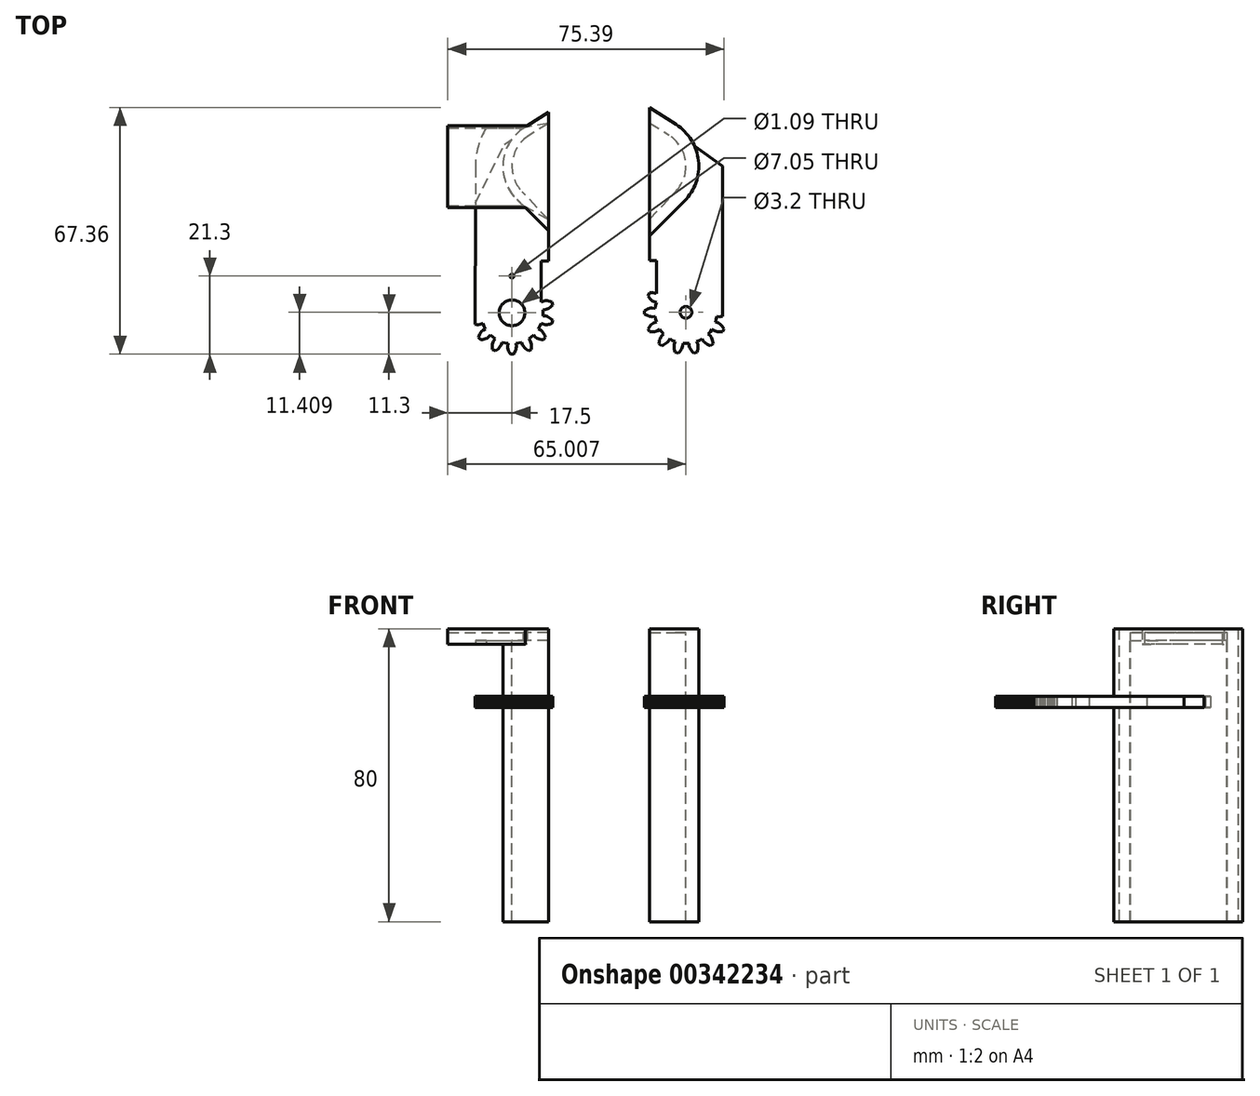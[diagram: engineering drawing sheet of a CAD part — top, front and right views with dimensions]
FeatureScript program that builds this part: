
annotation { "Feature Type Name" : "Feature", "Feature Type Description" : "" }
export const myFeature = defineFeature(function(context is Context, id is Id, definition is map)
    precondition{}
    {
        {
            var Q0;
            Q0=qCreatedBy(makeId("Top.planeOp"),FACE);
            var sketch = newSketch(context, id + "F0", { "sketchPlane" : qUnion([Q0])});
            skLineSegment(sketch, "E0", {"start": v(-11.89, -38.22) * mm, "end": v(-11.08, -38.37) * mm});
            skLineSegment(sketch, "E1", {"start": v(-11.08, -38.37) * mm, "end": v(-11.18, -39.18) * mm});
            skLineSegment(sketch, "E2", {"start": v(-11.18, -39.18) * mm, "end": v(-11.15, -39.59) * mm});
            skLineSegment(sketch, "E3", {"start": v(-11.15, -39.59) * mm, "end": v(-11.05, -40) * mm});
            skLineSegment(sketch, "E4", {"start": v(-11.05, -40) * mm, "end": v(-10.9, -40.42) * mm});
            skLineSegment(sketch, "E5", {"start": v(-10.9, -40.42) * mm, "end": v(-10.7, -40.84) * mm});
            skLineSegment(sketch, "E6", {"start": v(-10.7, -40.84) * mm, "end": v(-10.46, -41.25) * mm});
            skLineSegment(sketch, "E7", {"start": v(-10.46, -41.25) * mm, "end": v(-9.54, -41.25) * mm});
            skLineSegment(sketch, "E8", {"start": v(-9.54, -41.25) * mm, "end": v(-9.3, -40.84) * mm});
            skLineSegment(sketch, "E9", {"start": v(-9.3, -40.84) * mm, "end": v(-9.1, -40.42) * mm});
            skLineSegment(sketch, "E10", {"start": v(-9.1, -40.42) * mm, "end": v(-8.95, -40) * mm});
            skLineSegment(sketch, "E11", {"start": v(-8.95, -40) * mm, "end": v(-8.85, -39.59) * mm});
            skLineSegment(sketch, "E12", {"start": v(-8.85, -39.59) * mm, "end": v(-8.82, -39.18) * mm});
            skLineSegment(sketch, "E13", {"start": v(-8.82, -39.18) * mm, "end": v(-8.92, -38.37) * mm});
            skLineSegment(sketch, "E14", {"start": v(-8.92, -38.37) * mm, "end": v(-8.11, -38.22) * mm});
            skLineSegment(sketch, "E15", {"start": v(-8.11, -38.22) * mm, "end": v(-8.11, -38.22) * mm});
            skLineSegment(sketch, "E16", {"start": v(-8.11, -38.22) * mm, "end": v(-7.32, -38) * mm});
            skLineSegment(sketch, "E17", {"start": v(-7.32, -38) * mm, "end": v(-7.06, -38.78) * mm});
            skLineSegment(sketch, "E18", {"start": v(-7.06, -38.78) * mm, "end": v(-6.86, -39.13) * mm});
            skLineSegment(sketch, "E19", {"start": v(-6.86, -39.13) * mm, "end": v(-6.58, -39.46) * mm});
            skLineSegment(sketch, "E20", {"start": v(-6.58, -39.46) * mm, "end": v(-6.26, -39.77) * mm});
            skLineSegment(sketch, "E21", {"start": v(-6.26, -39.77) * mm, "end": v(-5.9, -40.06) * mm});
            skLineSegment(sketch, "E22", {"start": v(-5.9, -40.06) * mm, "end": v(-5.5, -40.33) * mm});
            skLineSegment(sketch, "E23", {"start": v(-5.5, -40.33) * mm, "end": v(-4.68, -39.94) * mm});
            skLineSegment(sketch, "E24", {"start": v(-4.68, -39.94) * mm, "end": v(-4.65, -39.46) * mm});
            skLineSegment(sketch, "E25", {"start": v(-4.65, -39.46) * mm, "end": v(-4.65, -39) * mm});
            skLineSegment(sketch, "E26", {"start": v(-4.7, -38.55) * mm, "end": v(-4.78, -38.13) * mm});
            skLineSegment(sketch, "E27", {"start": v(-4.78, -38.13) * mm, "end": v(-4.93, -37.75) * mm});
            skLineSegment(sketch, "E28", {"start": v(-4.93, -37.75) * mm, "end": v(-5.38, -37.07) * mm});
            skLineSegment(sketch, "E29", {"start": v(-4.09, -36.04) * mm, "end": v(-3.52, -36.62) * mm});
            skLineSegment(sketch, "E30", {"start": v(-3.18, -36.86) * mm, "end": v(-2.8, -37.04) * mm});
            skLineSegment(sketch, "E31", {"start": v(-2.37, -37.18) * mm, "end": v(-1.92, -37.28) * mm});
            skLineSegment(sketch, "E32", {"start": v(-1.05, -36.2) * mm, "end": v(-1.25, -35.78) * mm});
            skLineSegment(sketch, "E33", {"start": v(-1.25, -35.78) * mm, "end": v(-1.49, -35.4) * mm});
            skLineSegment(sketch, "E34", {"start": v(-2.05, -34.78) * mm, "end": v(-2.75, -34.36) * mm});
            skLineSegment(sketch, "E35", {"start": v(-2.03, -32.87) * mm, "end": v(-1.27, -33.15) * mm});
            skLineSegment(sketch, "E36", {"start": v(-20, -33.15) * mm, "end": v(-19.57, -33.2) * mm});
            skLineSegment(sketch, "E37", {"start": v(-19.57, -33.2) * mm, "end": v(-19.14, -33.22) * mm});
            skLineSegment(sketch, "E38", {"start": v(-19.14, -33.22) * mm, "end": v(-18.73, -33.15) * mm});
            skLineSegment(sketch, "E39", {"start": v(-18.73, -33.15) * mm, "end": v(-17.97, -32.87) * mm});
            skLineSegment(sketch, "E40", {"start": v(-17.97, -32.87) * mm, "end": v(-17.64, -33.63) * mm});
            skLineSegment(sketch, "E41", {"start": v(-17.64, -33.63) * mm, "end": v(-17.65, -33.63) * mm});
            skLineSegment(sketch, "E42", {"start": v(-17.65, -33.63) * mm, "end": v(-17.25, -34.36) * mm});
            skLineSegment(sketch, "E43", {"start": v(-17.25, -34.36) * mm, "end": v(-17.95, -34.78) * mm});
            skLineSegment(sketch, "E44", {"start": v(-17.95, -34.78) * mm, "end": v(-18.25, -35.06) * mm});
            skLineSegment(sketch, "E45", {"start": v(-18.25, -35.06) * mm, "end": v(-18.51, -35.4) * mm});
            skLineSegment(sketch, "E46", {"start": v(-18.51, -35.4) * mm, "end": v(-18.75, -35.78) * mm});
            skLineSegment(sketch, "E47", {"start": v(-18.75, -35.78) * mm, "end": v(-18.95, -36.2) * mm});
            skLineSegment(sketch, "E48", {"start": v(-18.95, -36.2) * mm, "end": v(-19.12, -36.64) * mm});
            skLineSegment(sketch, "E49", {"start": v(-19.12, -36.64) * mm, "end": v(-18.55, -37.36) * mm});
            skLineSegment(sketch, "E50", {"start": v(-18.55, -37.36) * mm, "end": v(-18.08, -37.28) * mm});
            skLineSegment(sketch, "E51", {"start": v(-18.08, -37.28) * mm, "end": v(-17.63, -37.18) * mm});
            skLineSegment(sketch, "E52", {"start": v(-17.63, -37.18) * mm, "end": v(-17.2, -37.04) * mm});
            skLineSegment(sketch, "E53", {"start": v(-17.2, -37.04) * mm, "end": v(-16.82, -36.86) * mm});
            skLineSegment(sketch, "E54", {"start": v(-16.82, -36.86) * mm, "end": v(-16.48, -36.62) * mm});
            skLineSegment(sketch, "E55", {"start": v(-16.48, -36.62) * mm, "end": v(-15.91, -36.04) * mm});
            skLineSegment(sketch, "E56", {"start": v(-15.91, -36.04) * mm, "end": v(-15.3, -36.58) * mm});
            skLineSegment(sketch, "E57", {"start": v(-15.3, -36.58) * mm, "end": v(-15.3, -36.58) * mm});
            skLineSegment(sketch, "E58", {"start": v(-15.3, -36.58) * mm, "end": v(-14.62, -37.07) * mm});
            skLineSegment(sketch, "E59", {"start": v(-14.62, -37.07) * mm, "end": v(-15.07, -37.75) * mm});
            skLineSegment(sketch, "E60", {"start": v(-15.07, -37.75) * mm, "end": v(-15.22, -38.13) * mm});
            skLineSegment(sketch, "E61", {"start": v(-15.22, -38.13) * mm, "end": v(-15.3, -38.55) * mm});
            skLineSegment(sketch, "E62", {"start": v(-15.3, -38.55) * mm, "end": v(-15.35, -39) * mm});
            skLineSegment(sketch, "E63", {"start": v(-15.35, -39) * mm, "end": v(-15.35, -39.46) * mm});
            skLineSegment(sketch, "E64", {"start": v(-15.35, -39.46) * mm, "end": v(-15.32, -39.94) * mm});
            skLineSegment(sketch, "E65", {"start": v(-15.32, -39.94) * mm, "end": v(-14.5, -40.33) * mm});
            skLineSegment(sketch, "E66", {"start": v(-14.5, -40.33) * mm, "end": v(-14.1, -40.06) * mm});
            skLineSegment(sketch, "E67", {"start": v(-14.1, -40.06) * mm, "end": v(-13.74, -39.77) * mm});
            skLineSegment(sketch, "E68", {"start": v(-13.74, -39.77) * mm, "end": v(-13.42, -39.46) * mm});
            skLineSegment(sketch, "E69", {"start": v(-13.42, -39.46) * mm, "end": v(-13.14, -39.13) * mm});
            skLineSegment(sketch, "E70", {"start": v(-13.14, -39.13) * mm, "end": v(-12.94, -38.78) * mm});
            skLineSegment(sketch, "E71", {"start": v(-12.94, -38.78) * mm, "end": v(-12.68, -38) * mm});
            skLineSegment(sketch, "E72", {"start": v(-12.68, -38) * mm, "end": v(-11.89, -38.22) * mm});
            skLineSegment(sketch, "E73", {"start": v(-11.89, -38.22) * mm, "end": v(-11.89, -38.22) * mm});
            skLineSegment(sketch, "E74", {"start": v(-2, -27.02) * mm, "end": v(-2, -15.8) * mm});
            skLineSegment(sketch, "E75", {"start": v(-4.65, -39) * mm, "end": v(-4.7, -38.55) * mm});
            skLineSegment(sketch, "E76", {"start": v(-5.38, -37.07) * mm, "end": v(-4.7, -36.58) * mm});
            skLineSegment(sketch, "E77", {"start": v(-4.7, -36.58) * mm, "end": v(-4.7, -36.58) * mm});
            skLineSegment(sketch, "E78", {"start": v(-4.7, -36.58) * mm, "end": v(-4.09, -36.04) * mm});
            skLineSegment(sketch, "E79", {"start": v(-3.52, -36.62) * mm, "end": v(-3.18, -36.86) * mm});
            skLineSegment(sketch, "E80", {"start": v(-2.8, -37.04) * mm, "end": v(-2.37, -37.18) * mm});
            skLineSegment(sketch, "E81", {"start": v(-1.92, -37.28) * mm, "end": v(-1.45, -37.36) * mm});
            skLineSegment(sketch, "E82", {"start": v(-1.45, -37.36) * mm, "end": v(-0.88, -36.64) * mm});
            skLineSegment(sketch, "E83", {"start": v(-0.88, -36.64) * mm, "end": v(-1.05, -36.2) * mm});
            skLineSegment(sketch, "E84", {"start": v(-1.49, -35.4) * mm, "end": v(-1.75, -35.06) * mm});
            skLineSegment(sketch, "E85", {"start": v(-1.75, -35.06) * mm, "end": v(-2.05, -34.78) * mm});
            skLineSegment(sketch, "E86", {"start": v(-2.75, -34.36) * mm, "end": v(-2.35, -33.63) * mm});
            skLineSegment(sketch, "E87", {"start": v(-2.35, -33.63) * mm, "end": v(-2.36, -33.63) * mm});
            skLineSegment(sketch, "E88", {"start": v(-2.36, -33.63) * mm, "end": v(-2.03, -32.87) * mm});
            skLineSegment(sketch, "E89", {"start": v(-1.27, -33.15) * mm, "end": v(-0.86, -33.22) * mm});
            skLineSegment(sketch, "E90", {"start": v(-0.86, -33.22) * mm, "end": v(-0.43, -33.2) * mm});
            skLineSegment(sketch, "E91", {"start": v(-0.43, -33.2) * mm, "end": v(0, -33.15) * mm});
            skLineSegment(sketch, "E92", {"start": v(0, -33.15) * mm, "end": v(0.46, -33.05) * mm});
            skLineSegment(sketch, "E93", {"start": v(0.46, -33.05) * mm, "end": v(0.92, -32.91) * mm});
            skLineSegment(sketch, "E94", {"start": v(0.92, -32.91) * mm, "end": v(1.12, -32.02) * mm});
            skLineSegment(sketch, "E95", {"start": v(1.12, -32.02) * mm, "end": v(0.77, -31.7) * mm});
            skLineSegment(sketch, "E96", {"start": v(0.77, -31.7) * mm, "end": v(0.4, -31.4) * mm});
            skLineSegment(sketch, "E97", {"start": v(0.4, -31.4) * mm, "end": v(0.03, -31.16) * mm});
            skLineSegment(sketch, "E98", {"start": v(0.03, -31.16) * mm, "end": v(-0.35, -30.97) * mm});
            skLineSegment(sketch, "E99", {"start": v(-0.35, -30.97) * mm, "end": v(-0.74, -30.85) * mm});
            skLineSegment(sketch, "E100", {"start": v(-0.74, -30.85) * mm, "end": v(-1.55, -30.77) * mm});
            skLineSegment(sketch, "E101", {"start": v(-1.55, -30.77) * mm, "end": v(-1.51, -29.95) * mm});
            skLineSegment(sketch, "E102", {"start": v(-1.51, -29.95) * mm, "end": v(-1.51, -29.95) * mm});
            skLineSegment(sketch, "E103", {"start": v(-1.51, -29.95) * mm, "end": v(-1.55, -29.13) * mm});
            skLineSegment(sketch, "E104", {"start": v(-1.55, -29.13) * mm, "end": v(-0.74, -29.05) * mm});
            skLineSegment(sketch, "E105", {"start": v(-0.74, -29.05) * mm, "end": v(-0.35, -28.93) * mm});
            skLineSegment(sketch, "E106", {"start": v(-0.35, -28.93) * mm, "end": v(0.03, -28.74) * mm});
            skLineSegment(sketch, "E107", {"start": v(0.03, -28.74) * mm, "end": v(0.4, -28.5) * mm});
            skLineSegment(sketch, "E108", {"start": v(0.4, -28.5) * mm, "end": v(0.77, -28.2) * mm});
            skLineSegment(sketch, "E109", {"start": v(0.77, -28.2) * mm, "end": v(1.12, -27.88) * mm});
            skLineSegment(sketch, "E110", {"start": v(1.12, -27.88) * mm, "end": v(0.92, -26.99) * mm});
            skLineSegment(sketch, "E111", {"start": v(0.92, -26.99) * mm, "end": v(0.46, -26.85) * mm});
            skLineSegment(sketch, "E112", {"start": v(0.46, -26.85) * mm, "end": v(0, -26.75) * mm});
            skLineSegment(sketch, "E113", {"start": v(0, -26.75) * mm, "end": v(-0.43, -26.69) * mm});
            skLineSegment(sketch, "E114", {"start": v(-0.43, -26.69) * mm, "end": v(-0.86, -26.68) * mm});
            skLineSegment(sketch, "E115", {"start": v(-0.86, -26.68) * mm, "end": v(-1.27, -26.75) * mm});
            skLineSegment(sketch, "E116", {"start": v(-1.27, -26.75) * mm, "end": v(-2, -27.02) * mm});
            skLineSegment(sketch, "E117", {"start": v(45.78, -31.73) * mm, "end": v(45.92, -30.92) * mm});
            skLineSegment(sketch, "E118", {"start": v(45.92, -30.92) * mm, "end": v(46.73, -31.02) * mm});
            skLineSegment(sketch, "E119", {"start": v(46.73, -31.02) * mm, "end": v(47.14, -31) * mm});
            skLineSegment(sketch, "E120", {"start": v(47.14, -31) * mm, "end": v(47.5, -30.9) * mm});
            skLineSegment(sketch, "E121", {"start": v(27.87, -31) * mm, "end": v(28.28, -31.02) * mm});
            skLineSegment(sketch, "E122", {"start": v(29.1, -30.92) * mm, "end": v(29.23, -31.73) * mm});
            skLineSegment(sketch, "E123", {"start": v(28.68, -32.78) * mm, "end": v(28.33, -32.99) * mm});
            skLineSegment(sketch, "E124", {"start": v(27.68, -33.58) * mm, "end": v(27.4, -33.94) * mm});
            skLineSegment(sketch, "E125", {"start": v(28.46, -35.2) * mm, "end": v(28.9, -35.15) * mm});
            skLineSegment(sketch, "E126", {"start": v(28.9, -35.15) * mm, "end": v(29.32, -35.06) * mm});
            skLineSegment(sketch, "E127", {"start": v(29.32, -35.06) * mm, "end": v(29.7, -34.9) * mm});
            skLineSegment(sketch, "E128", {"start": v(29.7, -34.9) * mm, "end": v(30.4, -34.46) * mm});
            skLineSegment(sketch, "E129", {"start": v(30.4, -34.46) * mm, "end": v(30.87, -35.13) * mm});
            skLineSegment(sketch, "E130", {"start": v(30.87, -35.13) * mm, "end": v(30.87, -35.13) * mm});
            skLineSegment(sketch, "E131", {"start": v(31.42, -35.75) * mm, "end": v(30.83, -36.32) * mm});
            skLineSegment(sketch, "E132", {"start": v(30.17, -37.92) * mm, "end": v(30.1, -38.4) * mm});
            skLineSegment(sketch, "E133", {"start": v(30.1, -38.4) * mm, "end": v(30.82, -38.96) * mm});
            skLineSegment(sketch, "E134", {"start": v(30.82, -38.96) * mm, "end": v(31.26, -38.8) * mm});
            skLineSegment(sketch, "E135", {"start": v(31.68, -38.59) * mm, "end": v(32.06, -38.35) * mm});
            skLineSegment(sketch, "E136", {"start": v(32.06, -38.35) * mm, "end": v(32.4, -38.1) * mm});
            skLineSegment(sketch, "E137", {"start": v(32.68, -37.8) * mm, "end": v(33.1, -37.1) * mm});
            skLineSegment(sketch, "E138", {"start": v(33.1, -37.1) * mm, "end": v(33.83, -37.49) * mm});
            skLineSegment(sketch, "E139", {"start": v(33.83, -37.49) * mm, "end": v(33.83, -37.49) * mm});
            skLineSegment(sketch, "E140", {"start": v(34.59, -37.8) * mm, "end": v(34.3, -38.58) * mm});
            skLineSegment(sketch, "E141", {"start": v(34.4, -40.3) * mm, "end": v(34.55, -40.76) * mm});
            skLineSegment(sketch, "E142", {"start": v(35.44, -40.96) * mm, "end": v(35.76, -40.61) * mm});
            skLineSegment(sketch, "E143", {"start": v(36.05, -40.25) * mm, "end": v(36.3, -39.88) * mm});
            skLineSegment(sketch, "E144", {"start": v(36.68, -38.29) * mm, "end": v(37.5, -38.33) * mm});
            skLineSegment(sketch, "E145", {"start": v(37.5, -38.33) * mm, "end": v(37.5, -38.33) * mm});
            skLineSegment(sketch, "E146", {"start": v(37.5, -38.33) * mm, "end": v(38.33, -38.29) * mm});
            skLineSegment(sketch, "E147", {"start": v(38.33, -38.29) * mm, "end": v(38.41, -39.1) * mm});
            skLineSegment(sketch, "E148", {"start": v(38.41, -39.1) * mm, "end": v(38.53, -39.5) * mm});
            skLineSegment(sketch, "E149", {"start": v(38.53, -39.5) * mm, "end": v(38.72, -39.88) * mm});
            skLineSegment(sketch, "E150", {"start": v(38.72, -39.88) * mm, "end": v(38.96, -40.25) * mm});
            skLineSegment(sketch, "E151", {"start": v(38.96, -40.25) * mm, "end": v(39.25, -40.61) * mm});
            skLineSegment(sketch, "E152", {"start": v(39.25, -40.61) * mm, "end": v(39.58, -40.96) * mm});
            skLineSegment(sketch, "E153", {"start": v(39.58, -40.96) * mm, "end": v(40.47, -40.76) * mm});
            skLineSegment(sketch, "E154", {"start": v(40.47, -40.76) * mm, "end": v(40.61, -40.3) * mm});
            skLineSegment(sketch, "E155", {"start": v(40.61, -40.3) * mm, "end": v(40.71, -39.85) * mm});
            skLineSegment(sketch, "E156", {"start": v(40.71, -39.85) * mm, "end": v(40.77, -39.4) * mm});
            skLineSegment(sketch, "E157", {"start": v(40.77, -39.4) * mm, "end": v(40.77, -38.98) * mm});
            skLineSegment(sketch, "E158", {"start": v(40.77, -38.98) * mm, "end": v(40.7, -38.58) * mm});
            skLineSegment(sketch, "E159", {"start": v(40.7, -38.58) * mm, "end": v(40.43, -37.8) * mm});
            skLineSegment(sketch, "E160", {"start": v(40.43, -37.8) * mm, "end": v(41.19, -37.49) * mm});
            skLineSegment(sketch, "E161", {"start": v(41.19, -37.49) * mm, "end": v(41.19, -37.49) * mm});
            skLineSegment(sketch, "E162", {"start": v(41.19, -37.49) * mm, "end": v(41.91, -37.1) * mm});
            skLineSegment(sketch, "E163", {"start": v(41.91, -37.1) * mm, "end": v(42.34, -37.8) * mm});
            skLineSegment(sketch, "E164", {"start": v(42.34, -37.8) * mm, "end": v(42.62, -38.1) * mm});
            skLineSegment(sketch, "E165", {"start": v(42.62, -38.1) * mm, "end": v(42.95, -38.35) * mm});
            skLineSegment(sketch, "E166", {"start": v(42.95, -38.35) * mm, "end": v(43.33, -38.59) * mm});
            skLineSegment(sketch, "E167", {"start": v(43.33, -38.59) * mm, "end": v(43.75, -38.8) * mm});
            skLineSegment(sketch, "E168", {"start": v(43.75, -38.8) * mm, "end": v(44.2, -38.96) * mm});
            skLineSegment(sketch, "E169", {"start": v(44.2, -38.96) * mm, "end": v(44.91, -38.4) * mm});
            skLineSegment(sketch, "E170", {"start": v(44.91, -38.4) * mm, "end": v(44.84, -37.92) * mm});
            skLineSegment(sketch, "E171", {"start": v(44.84, -37.92) * mm, "end": v(44.74, -37.47) * mm});
            skLineSegment(sketch, "E172", {"start": v(44.74, -37.47) * mm, "end": v(44.6, -37.05) * mm});
            skLineSegment(sketch, "E173", {"start": v(44.6, -37.05) * mm, "end": v(44.41, -36.66) * mm});
            skLineSegment(sketch, "E174", {"start": v(44.41, -36.66) * mm, "end": v(44.18, -36.32) * mm});
            skLineSegment(sketch, "E175", {"start": v(44.18, -36.32) * mm, "end": v(43.6, -35.75) * mm});
            skLineSegment(sketch, "E176", {"start": v(43.6, -35.75) * mm, "end": v(44.14, -35.13) * mm});
            skLineSegment(sketch, "E177", {"start": v(44.14, -35.13) * mm, "end": v(44.14, -35.13) * mm});
            skLineSegment(sketch, "E178", {"start": v(44.14, -35.13) * mm, "end": v(44.62, -34.46) * mm});
            skLineSegment(sketch, "E179", {"start": v(44.62, -34.46) * mm, "end": v(45.3, -34.9) * mm});
            skLineSegment(sketch, "E180", {"start": v(45.3, -34.9) * mm, "end": v(45.69, -35.06) * mm});
            skLineSegment(sketch, "E181", {"start": v(45.69, -35.06) * mm, "end": v(46.1, -35.15) * mm});
            skLineSegment(sketch, "E182", {"start": v(46.1, -35.15) * mm, "end": v(46.55, -35.2) * mm});
            skLineSegment(sketch, "E183", {"start": v(46.55, -35.2) * mm, "end": v(47.01, -35.2) * mm});
            skLineSegment(sketch, "E184", {"start": v(47.01, -35.2) * mm, "end": v(47.5, -35.16) * mm});
            skLineSegment(sketch, "E185", {"start": v(47.5, -35.16) * mm, "end": v(47.9, -34.33) * mm});
            skLineSegment(sketch, "E186", {"start": v(47.9, -34.33) * mm, "end": v(47.62, -33.94) * mm});
            skLineSegment(sketch, "E187", {"start": v(47.62, -33.94) * mm, "end": v(47.33, -33.58) * mm});
            skLineSegment(sketch, "E188", {"start": v(47.33, -33.58) * mm, "end": v(47.02, -33.26) * mm});
            skLineSegment(sketch, "E189", {"start": v(47.02, -33.26) * mm, "end": v(46.69, -32.99) * mm});
            skLineSegment(sketch, "E190", {"start": v(46.69, -32.99) * mm, "end": v(46.33, -32.78) * mm});
            skLineSegment(sketch, "E191", {"start": v(46.33, -32.78) * mm, "end": v(45.56, -32.52) * mm});
            skLineSegment(sketch, "E192", {"start": v(45.56, -32.52) * mm, "end": v(45.78, -31.73) * mm});
            skLineSegment(sketch, "E193", {"start": v(45.78, -31.73) * mm, "end": v(45.78, -31.73) * mm});
            skLineSegment(sketch, "E194", {"start": v(29.5, -24.7) * mm, "end": v(29.5, -15.7) * mm});
            skLineSegment(sketch, "E195", {"start": v(47.5, -30.9) * mm, "end": v(47.5, 10.1) * mm});
            skLineSegment(sketch, "E196", {"start": v(29.5, -24.7) * mm, "end": v(29.32, -24.62) * mm});
            skLineSegment(sketch, "E197", {"start": v(29.32, -24.62) * mm, "end": v(28.9, -24.53) * mm});
            skLineSegment(sketch, "E198", {"start": v(28.9, -24.53) * mm, "end": v(28.46, -24.5) * mm});
            skLineSegment(sketch, "E199", {"start": v(28.46, -24.5) * mm, "end": v(28, -24.49) * mm});
            skLineSegment(sketch, "E200", {"start": v(28, -24.49) * mm, "end": v(27.52, -24.53) * mm});
            skLineSegment(sketch, "E201", {"start": v(27.52, -24.53) * mm, "end": v(27.12, -25.35) * mm});
            skLineSegment(sketch, "E202", {"start": v(27.12, -25.35) * mm, "end": v(27.4, -25.75) * mm});
            skLineSegment(sketch, "E203", {"start": v(27.4, -25.75) * mm, "end": v(27.68, -26.1) * mm});
            skLineSegment(sketch, "E204", {"start": v(27.68, -26.1) * mm, "end": v(28, -26.43) * mm});
            skLineSegment(sketch, "E205", {"start": v(28, -26.43) * mm, "end": v(28.33, -26.7) * mm});
            skLineSegment(sketch, "E206", {"start": v(28.33, -26.7) * mm, "end": v(28.68, -26.9) * mm});
            skLineSegment(sketch, "E207", {"start": v(28.68, -26.9) * mm, "end": v(29.46, -27.16) * mm});
            skLineSegment(sketch, "E208", {"start": v(29.46, -27.16) * mm, "end": v(29.23, -27.95) * mm});
            skLineSegment(sketch, "E209", {"start": v(29.23, -27.95) * mm, "end": v(29.23, -27.95) * mm});
            skLineSegment(sketch, "E210", {"start": v(29.23, -27.95) * mm, "end": v(29.1, -28.77) * mm});
            skLineSegment(sketch, "E211", {"start": v(29.1, -28.77) * mm, "end": v(28.28, -28.66) * mm});
            skLineSegment(sketch, "E212", {"start": v(28.28, -28.66) * mm, "end": v(27.87, -28.7) * mm});
            skLineSegment(sketch, "E213", {"start": v(27.87, -28.7) * mm, "end": v(27.45, -28.8) * mm});
            skLineSegment(sketch, "E214", {"start": v(27.45, -28.8) * mm, "end": v(27.04, -28.94) * mm});
            skLineSegment(sketch, "E215", {"start": v(27.04, -28.94) * mm, "end": v(26.62, -29.14) * mm});
            skLineSegment(sketch, "E216", {"start": v(26.62, -29.14) * mm, "end": v(26.2, -29.38) * mm});
            skLineSegment(sketch, "E217", {"start": v(26.2, -30.3) * mm, "end": v(26.62, -30.54) * mm});
            skLineSegment(sketch, "E218", {"start": v(26.62, -30.54) * mm, "end": v(27.04, -30.74) * mm});
            skLineSegment(sketch, "E219", {"start": v(27.04, -30.74) * mm, "end": v(27.45, -30.9) * mm});
            skLineSegment(sketch, "E220", {"start": v(27.45, -30.9) * mm, "end": v(27.87, -31) * mm});
            skLineSegment(sketch, "E221", {"start": v(28.28, -31.02) * mm, "end": v(29.1, -30.92) * mm});
            skLineSegment(sketch, "E222", {"start": v(29.23, -31.73) * mm, "end": v(29.23, -31.73) * mm});
            skLineSegment(sketch, "E223", {"start": v(29.23, -31.73) * mm, "end": v(29.46, -32.52) * mm});
            skLineSegment(sketch, "E224", {"start": v(29.46, -32.52) * mm, "end": v(28.68, -32.78) * mm});
            skLineSegment(sketch, "E225", {"start": v(28.33, -32.99) * mm, "end": v(28, -33.26) * mm});
            skLineSegment(sketch, "E226", {"start": v(28, -33.26) * mm, "end": v(27.68, -33.58) * mm});
            skLineSegment(sketch, "E227", {"start": v(27.4, -33.94) * mm, "end": v(27.12, -34.33) * mm});
            skLineSegment(sketch, "E228", {"start": v(27.12, -34.33) * mm, "end": v(27.52, -35.16) * mm});
            skLineSegment(sketch, "E229", {"start": v(27.52, -35.16) * mm, "end": v(28, -35.2) * mm});
            skLineSegment(sketch, "E230", {"start": v(28, -35.2) * mm, "end": v(28.46, -35.2) * mm});
            skLineSegment(sketch, "E231", {"start": v(30.87, -35.13) * mm, "end": v(31.42, -35.75) * mm});
            skLineSegment(sketch, "E232", {"start": v(30.83, -36.32) * mm, "end": v(30.6, -36.66) * mm});
            skLineSegment(sketch, "E233", {"start": v(30.6, -36.66) * mm, "end": v(30.42, -37.05) * mm});
            skLineSegment(sketch, "E234", {"start": v(30.42, -37.05) * mm, "end": v(30.28, -37.47) * mm});
            skLineSegment(sketch, "E235", {"start": v(30.28, -37.47) * mm, "end": v(30.17, -37.92) * mm});
            skLineSegment(sketch, "E236", {"start": v(31.26, -38.8) * mm, "end": v(31.68, -38.59) * mm});
            skLineSegment(sketch, "E237", {"start": v(32.4, -38.1) * mm, "end": v(32.68, -37.8) * mm});
            skLineSegment(sketch, "E238", {"start": v(33.83, -37.49) * mm, "end": v(34.59, -37.8) * mm});
            skLineSegment(sketch, "E239", {"start": v(34.3, -38.58) * mm, "end": v(34.24, -38.98) * mm});
            skLineSegment(sketch, "E240", {"start": v(34.24, -38.98) * mm, "end": v(34.25, -39.4) * mm});
            skLineSegment(sketch, "E241", {"start": v(34.25, -39.4) * mm, "end": v(34.3, -39.85) * mm});
            skLineSegment(sketch, "E242", {"start": v(34.3, -39.85) * mm, "end": v(34.4, -40.3) * mm});
            skLineSegment(sketch, "E243", {"start": v(34.55, -40.76) * mm, "end": v(35.44, -40.96) * mm});
            skLineSegment(sketch, "E244", {"start": v(35.76, -40.61) * mm, "end": v(36.05, -40.25) * mm});
            skLineSegment(sketch, "E245", {"start": v(36.3, -39.88) * mm, "end": v(36.48, -39.5) * mm});
            skLineSegment(sketch, "E246", {"start": v(36.48, -39.5) * mm, "end": v(36.6, -39.1) * mm});
            skLineSegment(sketch, "E247", {"start": v(36.6, -39.1) * mm, "end": v(36.68, -38.29) * mm});
            skLineSegment(sketch, "E248", {"start": v(26.2, -29.38) * mm, "end": v(26.2, -30.3) * mm});
            skCircle(sketch, "E249", {"center": v(37.5, -29.84) * mm, "radius": 1.6 * mm});
            skCircle(sketch, "E250", {"center": v(-10, -29.95) * mm, "radius": 3.52 * mm});
            skCircle(sketch, "E251", {"center": v(-10, -19.95) * mm, "radius": 0.55 * mm});
            skLineSegment(sketch, "E252", {"start": v(97.08, -42.45) * mm, "end": v(97.9, -42.59) * mm});
            skLineSegment(sketch, "E253", {"start": v(97.9, -42.59) * mm, "end": v(97.8, -43.4) * mm});
            skLineSegment(sketch, "E254", {"start": v(97.8, -43.4) * mm, "end": v(97.82, -43.8) * mm});
            skLineSegment(sketch, "E255", {"start": v(97.82, -43.8) * mm, "end": v(97.92, -44.23) * mm});
            skLineSegment(sketch, "E256", {"start": v(97.92, -44.23) * mm, "end": v(98.07, -44.64) * mm});
            skLineSegment(sketch, "E257", {"start": v(98.07, -44.64) * mm, "end": v(98.27, -45.06) * mm});
            skLineSegment(sketch, "E258", {"start": v(98.27, -45.06) * mm, "end": v(98.51, -45.48) * mm});
            skLineSegment(sketch, "E259", {"start": v(98.51, -45.48) * mm, "end": v(99.43, -45.48) * mm});
            skLineSegment(sketch, "E260", {"start": v(99.43, -45.48) * mm, "end": v(99.67, -45.06) * mm});
            skLineSegment(sketch, "E261", {"start": v(99.67, -45.06) * mm, "end": v(99.87, -44.64) * mm});
            skLineSegment(sketch, "E262", {"start": v(99.87, -44.64) * mm, "end": v(100.02, -44.23) * mm});
            skLineSegment(sketch, "E263", {"start": v(100.02, -44.23) * mm, "end": v(100.12, -43.8) * mm});
            skLineSegment(sketch, "E264", {"start": v(100.12, -43.8) * mm, "end": v(100.15, -43.4) * mm});
            skLineSegment(sketch, "E265", {"start": v(100.15, -43.4) * mm, "end": v(100.05, -42.59) * mm});
            skLineSegment(sketch, "E266", {"start": v(100.05, -42.59) * mm, "end": v(100.86, -42.45) * mm});
            skLineSegment(sketch, "E267", {"start": v(100.86, -42.45) * mm, "end": v(100.86, -42.45) * mm});
            skLineSegment(sketch, "E268", {"start": v(100.86, -42.45) * mm, "end": v(101.65, -42.22) * mm});
            skLineSegment(sketch, "E269", {"start": v(101.65, -42.22) * mm, "end": v(101.91, -43) * mm});
            skLineSegment(sketch, "E270", {"start": v(101.91, -43) * mm, "end": v(102.12, -43.35) * mm});
            skLineSegment(sketch, "E271", {"start": v(102.12, -43.35) * mm, "end": v(102.39, -43.68) * mm});
            skLineSegment(sketch, "E272", {"start": v(102.39, -43.68) * mm, "end": v(102.7, -44) * mm});
            skLineSegment(sketch, "E273", {"start": v(102.7, -44) * mm, "end": v(103.07, -44.29) * mm});
            skLineSegment(sketch, "E274", {"start": v(103.07, -44.29) * mm, "end": v(103.46, -44.56) * mm});
            skLineSegment(sketch, "E275", {"start": v(103.46, -44.56) * mm, "end": v(104.29, -44.16) * mm});
            skLineSegment(sketch, "E276", {"start": v(104.29, -44.16) * mm, "end": v(104.32, -43.68) * mm});
            skLineSegment(sketch, "E277", {"start": v(104.32, -43.68) * mm, "end": v(104.32, -43.22) * mm});
            skLineSegment(sketch, "E278", {"start": v(104.28, -42.77) * mm, "end": v(104.19, -42.36) * mm});
            skLineSegment(sketch, "E279", {"start": v(104.19, -42.36) * mm, "end": v(104.04, -41.97) * mm});
            skLineSegment(sketch, "E280", {"start": v(104.04, -41.97) * mm, "end": v(103.6, -41.29) * mm});
            skLineSegment(sketch, "E281", {"start": v(104.88, -40.26) * mm, "end": v(105.45, -40.85) * mm});
            skLineSegment(sketch, "E282", {"start": v(105.79, -41.08) * mm, "end": v(106.18, -41.26) * mm});
            skLineSegment(sketch, "E283", {"start": v(106.6, -41.4) * mm, "end": v(107.05, -41.5) * mm});
            skLineSegment(sketch, "E284", {"start": v(107.92, -40.42) * mm, "end": v(107.72, -40) * mm});
            skLineSegment(sketch, "E285", {"start": v(107.72, -40) * mm, "end": v(107.48, -39.62) * mm});
            skLineSegment(sketch, "E286", {"start": v(106.92, -39) * mm, "end": v(106.22, -38.58) * mm});
            skLineSegment(sketch, "E287", {"start": v(106.94, -37.1) * mm, "end": v(107.7, -37.38) * mm});
            skLineSegment(sketch, "E288", {"start": v(88.96, -37.38) * mm, "end": v(89.4, -37.43) * mm});
            skLineSegment(sketch, "E289", {"start": v(89.4, -37.43) * mm, "end": v(89.83, -37.44) * mm});
            skLineSegment(sketch, "E290", {"start": v(89.83, -37.44) * mm, "end": v(90.24, -37.38) * mm});
            skLineSegment(sketch, "E291", {"start": v(90.24, -37.38) * mm, "end": v(91, -37.1) * mm});
            skLineSegment(sketch, "E292", {"start": v(91, -37.1) * mm, "end": v(91.33, -37.85) * mm});
            skLineSegment(sketch, "E293", {"start": v(91.33, -37.85) * mm, "end": v(91.33, -37.85) * mm});
            skLineSegment(sketch, "E294", {"start": v(91.33, -37.85) * mm, "end": v(91.72, -38.58) * mm});
            skLineSegment(sketch, "E295", {"start": v(91.72, -38.58) * mm, "end": v(91.02, -39) * mm});
            skLineSegment(sketch, "E296", {"start": v(91.02, -39) * mm, "end": v(90.72, -39.28) * mm});
            skLineSegment(sketch, "E297", {"start": v(90.72, -39.28) * mm, "end": v(90.46, -39.62) * mm});
            skLineSegment(sketch, "E298", {"start": v(90.46, -39.62) * mm, "end": v(90.23, -40) * mm});
            skLineSegment(sketch, "E299", {"start": v(90.23, -40) * mm, "end": v(90.02, -40.42) * mm});
            skLineSegment(sketch, "E300", {"start": v(90.02, -40.42) * mm, "end": v(89.85, -40.86) * mm});
            skLineSegment(sketch, "E301", {"start": v(89.85, -40.86) * mm, "end": v(90.42, -41.58) * mm});
            skLineSegment(sketch, "E302", {"start": v(90.42, -41.58) * mm, "end": v(90.9, -41.5) * mm});
            skLineSegment(sketch, "E303", {"start": v(90.9, -41.5) * mm, "end": v(91.34, -41.4) * mm});
            skLineSegment(sketch, "E304", {"start": v(91.34, -41.4) * mm, "end": v(91.77, -41.26) * mm});
            skLineSegment(sketch, "E305", {"start": v(91.77, -41.26) * mm, "end": v(92.15, -41.08) * mm});
            skLineSegment(sketch, "E306", {"start": v(92.15, -41.08) * mm, "end": v(92.5, -40.85) * mm});
            skLineSegment(sketch, "E307", {"start": v(92.5, -40.85) * mm, "end": v(93.06, -40.26) * mm});
            skLineSegment(sketch, "E308", {"start": v(93.06, -40.26) * mm, "end": v(93.68, -40.8) * mm});
            skLineSegment(sketch, "E309", {"start": v(93.68, -40.8) * mm, "end": v(93.68, -40.8) * mm});
            skLineSegment(sketch, "E310", {"start": v(93.68, -40.8) * mm, "end": v(94.35, -41.29) * mm});
            skLineSegment(sketch, "E311", {"start": v(94.35, -41.29) * mm, "end": v(93.9, -41.97) * mm});
            skLineSegment(sketch, "E312", {"start": v(93.9, -41.97) * mm, "end": v(93.75, -42.36) * mm});
            skLineSegment(sketch, "E313", {"start": v(93.75, -42.36) * mm, "end": v(93.66, -42.77) * mm});
            skLineSegment(sketch, "E314", {"start": v(93.66, -42.77) * mm, "end": v(93.62, -43.22) * mm});
            skLineSegment(sketch, "E315", {"start": v(93.62, -43.22) * mm, "end": v(93.62, -43.68) * mm});
            skLineSegment(sketch, "E316", {"start": v(93.62, -43.68) * mm, "end": v(93.65, -44.16) * mm});
            skLineSegment(sketch, "E317", {"start": v(93.65, -44.16) * mm, "end": v(94.48, -44.56) * mm});
            skLineSegment(sketch, "E318", {"start": v(94.48, -44.56) * mm, "end": v(94.87, -44.29) * mm});
            skLineSegment(sketch, "E319", {"start": v(94.87, -44.29) * mm, "end": v(95.24, -44) * mm});
            skLineSegment(sketch, "E320", {"start": v(95.24, -44) * mm, "end": v(95.55, -43.68) * mm});
            skLineSegment(sketch, "E321", {"start": v(95.55, -43.68) * mm, "end": v(95.83, -43.35) * mm});
            skLineSegment(sketch, "E322", {"start": v(95.83, -43.35) * mm, "end": v(96.03, -43) * mm});
            skLineSegment(sketch, "E323", {"start": v(96.03, -43) * mm, "end": v(96.29, -42.22) * mm});
            skLineSegment(sketch, "E324", {"start": v(96.29, -42.22) * mm, "end": v(97.08, -42.45) * mm});
            skLineSegment(sketch, "E325", {"start": v(97.08, -42.45) * mm, "end": v(97.08, -42.45) * mm});
            skLineSegment(sketch, "E326", {"start": v(98.97, -2.1) * mm, "end": v(98.97, 13.76) * mm});
            skArc(sketch, "E327", {"start": v(98.97, -2.1) * mm, "mid": v(99.35, -4.02) * mm, "end": v(100.44, -5.64) * mm});
            skLineSegment(sketch, "E328", {"start": v(106.97, -31.24) * mm, "end": v(106.97, -14.24) * mm});
            skArc(sketch, "E329", {"start": v(106.97, -14.24) * mm, "mid": v(106.6, -12.33) * mm, "end": v(105.5, -10.7) * mm});
            skLineSegment(sketch, "E330", {"start": v(108.97, 25.83) * mm, "end": v(108.97, 40.83) * mm});
            skLineSegment(sketch, "E331", {"start": v(108.97, 40.83) * mm, "end": v(106.04, 40.83) * mm});
            skArc(sketch, "E332", {"start": v(106.04, 40.83) * mm, "mid": v(104.13, 40.45) * mm, "end": v(102.5, 39.36) * mm});
            skLineSegment(sketch, "E333", {"start": v(88.96, -37.38) * mm, "end": v(88.97, 23.76) * mm});
            skLineSegment(sketch, "E334", {"start": v(102.5, 39.36) * mm, "end": v(90.43, 27.3) * mm});
            skArc(sketch, "E335", {"start": v(90.43, 27.3) * mm, "mid": v(89.35, 25.67) * mm, "end": v(88.97, 23.76) * mm});
            skLineSegment(sketch, "E336", {"start": v(108.97, 25.83) * mm, "end": v(100.44, 17.3) * mm});
            skArc(sketch, "E337", {"start": v(100.44, 17.3) * mm, "mid": v(99.35, 15.67) * mm, "end": v(98.97, 13.76) * mm});
            skLineSegment(sketch, "E338", {"start": v(100.44, -5.64) * mm, "end": v(105.5, -10.7) * mm});
            skLineSegment(sketch, "E339", {"start": v(104.32, -43.22) * mm, "end": v(104.28, -42.77) * mm});
            skLineSegment(sketch, "E340", {"start": v(103.6, -41.29) * mm, "end": v(104.26, -40.8) * mm});
            skLineSegment(sketch, "E341", {"start": v(104.26, -40.8) * mm, "end": v(104.26, -40.8) * mm});
            skLineSegment(sketch, "E342", {"start": v(104.26, -40.8) * mm, "end": v(104.88, -40.26) * mm});
            skLineSegment(sketch, "E343", {"start": v(105.45, -40.85) * mm, "end": v(105.79, -41.08) * mm});
            skLineSegment(sketch, "E344", {"start": v(106.18, -41.26) * mm, "end": v(106.6, -41.4) * mm});
            skLineSegment(sketch, "E345", {"start": v(107.05, -41.5) * mm, "end": v(107.52, -41.58) * mm});
            skLineSegment(sketch, "E346", {"start": v(107.52, -41.58) * mm, "end": v(108.1, -40.86) * mm});
            skLineSegment(sketch, "E347", {"start": v(108.1, -40.86) * mm, "end": v(107.92, -40.42) * mm});
            skLineSegment(sketch, "E348", {"start": v(107.48, -39.62) * mm, "end": v(107.22, -39.28) * mm});
            skLineSegment(sketch, "E349", {"start": v(107.22, -39.28) * mm, "end": v(106.92, -39) * mm});
            skLineSegment(sketch, "E350", {"start": v(106.22, -38.58) * mm, "end": v(106.62, -37.85) * mm});
            skLineSegment(sketch, "E351", {"start": v(106.62, -37.85) * mm, "end": v(106.62, -37.85) * mm});
            skLineSegment(sketch, "E352", {"start": v(106.62, -37.85) * mm, "end": v(106.94, -37.1) * mm});
            skLineSegment(sketch, "E353", {"start": v(107.7, -37.38) * mm, "end": v(108.1, -37.44) * mm});
            skLineSegment(sketch, "E354", {"start": v(108.1, -37.44) * mm, "end": v(108.54, -37.43) * mm});
            skLineSegment(sketch, "E355", {"start": v(108.54, -37.43) * mm, "end": v(108.98, -37.38) * mm});
            skLineSegment(sketch, "E356", {"start": v(108.98, -37.38) * mm, "end": v(109.43, -37.28) * mm});
            skLineSegment(sketch, "E357", {"start": v(109.43, -37.28) * mm, "end": v(109.9, -37.13) * mm});
            skLineSegment(sketch, "E358", {"start": v(109.9, -37.13) * mm, "end": v(110.1, -36.24) * mm});
            skLineSegment(sketch, "E359", {"start": v(110.1, -36.24) * mm, "end": v(109.74, -35.92) * mm});
            skLineSegment(sketch, "E360", {"start": v(109.74, -35.92) * mm, "end": v(109.38, -35.63) * mm});
            skLineSegment(sketch, "E361", {"start": v(109.38, -35.63) * mm, "end": v(109, -35.39) * mm});
            skLineSegment(sketch, "E362", {"start": v(109, -35.39) * mm, "end": v(108.62, -35.2) * mm});
            skLineSegment(sketch, "E363", {"start": v(108.62, -35.2) * mm, "end": v(108.23, -35.08) * mm});
            skLineSegment(sketch, "E364", {"start": v(108.23, -35.08) * mm, "end": v(107.42, -35) * mm});
            skLineSegment(sketch, "E365", {"start": v(107.42, -35) * mm, "end": v(107.46, -34.17) * mm});
            skLineSegment(sketch, "E366", {"start": v(107.46, -34.17) * mm, "end": v(107.46, -34.17) * mm});
            skLineSegment(sketch, "E367", {"start": v(107.46, -34.17) * mm, "end": v(107.42, -33.35) * mm});
            skLineSegment(sketch, "E368", {"start": v(107.42, -33.35) * mm, "end": v(108.23, -33.27) * mm});
            skLineSegment(sketch, "E369", {"start": v(108.23, -33.27) * mm, "end": v(108.62, -33.15) * mm});
            skLineSegment(sketch, "E370", {"start": v(108.62, -33.15) * mm, "end": v(109, -32.96) * mm});
            skLineSegment(sketch, "E371", {"start": v(109, -32.96) * mm, "end": v(109.38, -32.72) * mm});
            skLineSegment(sketch, "E372", {"start": v(109.38, -32.72) * mm, "end": v(109.74, -32.43) * mm});
            skLineSegment(sketch, "E373", {"start": v(109.74, -32.43) * mm, "end": v(110.1, -32.1) * mm});
            skLineSegment(sketch, "E374", {"start": v(110.1, -32.1) * mm, "end": v(109.9, -31.21) * mm});
            skLineSegment(sketch, "E375", {"start": v(109.9, -31.21) * mm, "end": v(109.43, -31.07) * mm});
            skLineSegment(sketch, "E376", {"start": v(109.43, -31.07) * mm, "end": v(108.98, -30.97) * mm});
            skLineSegment(sketch, "E377", {"start": v(108.98, -30.97) * mm, "end": v(108.54, -30.91) * mm});
            skLineSegment(sketch, "E378", {"start": v(108.54, -30.91) * mm, "end": v(108.1, -30.9) * mm});
            skLineSegment(sketch, "E379", {"start": v(108.1, -30.9) * mm, "end": v(107.7, -30.97) * mm});
            skLineSegment(sketch, "E380", {"start": v(107.7, -30.97) * mm, "end": v(106.97, -31.24) * mm});
            skLineSegment(sketch, "E381", {"start": v(150.9, -35.72) * mm, "end": v(151.04, -34.9) * mm});
            skLineSegment(sketch, "E382", {"start": v(151.04, -34.9) * mm, "end": v(151.85, -35) * mm});
            skLineSegment(sketch, "E383", {"start": v(151.85, -35) * mm, "end": v(152.25, -34.98) * mm});
            skLineSegment(sketch, "E384", {"start": v(152.25, -34.98) * mm, "end": v(152.62, -34.89) * mm});
            skLineSegment(sketch, "E385", {"start": v(132.98, -34.98) * mm, "end": v(133.4, -35) * mm});
            skLineSegment(sketch, "E386", {"start": v(134.2, -34.9) * mm, "end": v(134.35, -35.72) * mm});
            skLineSegment(sketch, "E387", {"start": v(133.8, -36.77) * mm, "end": v(133.44, -36.97) * mm});
            skLineSegment(sketch, "E388", {"start": v(132.8, -37.56) * mm, "end": v(132.5, -37.92) * mm});
            skLineSegment(sketch, "E389", {"start": v(133.57, -39.18) * mm, "end": v(134.02, -39.13) * mm});
            skLineSegment(sketch, "E390", {"start": v(134.02, -39.13) * mm, "end": v(134.44, -39.04) * mm});
            skLineSegment(sketch, "E391", {"start": v(134.44, -39.04) * mm, "end": v(134.82, -38.9) * mm});
            skLineSegment(sketch, "E392", {"start": v(134.82, -38.9) * mm, "end": v(135.5, -38.45) * mm});
            skLineSegment(sketch, "E393", {"start": v(135.5, -38.45) * mm, "end": v(135.98, -39.12) * mm});
            skLineSegment(sketch, "E394", {"start": v(135.98, -39.12) * mm, "end": v(135.98, -39.12) * mm});
            skLineSegment(sketch, "E395", {"start": v(136.53, -39.74) * mm, "end": v(135.94, -40.3) * mm});
            skLineSegment(sketch, "E396", {"start": v(135.28, -41.9) * mm, "end": v(135.21, -42.38) * mm});
            skLineSegment(sketch, "E397", {"start": v(135.21, -42.38) * mm, "end": v(135.93, -42.95) * mm});
            skLineSegment(sketch, "E398", {"start": v(135.93, -42.95) * mm, "end": v(136.37, -42.78) * mm});
            skLineSegment(sketch, "E399", {"start": v(136.8, -42.57) * mm, "end": v(137.17, -42.34) * mm});
            skLineSegment(sketch, "E400", {"start": v(137.17, -42.34) * mm, "end": v(137.5, -42.08) * mm});
            skLineSegment(sketch, "E401", {"start": v(137.79, -41.78) * mm, "end": v(138.21, -41.08) * mm});
            skLineSegment(sketch, "E402", {"start": v(138.21, -41.08) * mm, "end": v(138.94, -41.47) * mm});
            skLineSegment(sketch, "E403", {"start": v(138.94, -41.47) * mm, "end": v(138.94, -41.47) * mm});
            skLineSegment(sketch, "E404", {"start": v(139.7, -41.8) * mm, "end": v(139.42, -42.56) * mm});
            skLineSegment(sketch, "E405", {"start": v(139.51, -44.29) * mm, "end": v(139.66, -44.75) * mm});
            skLineSegment(sketch, "E406", {"start": v(140.55, -44.95) * mm, "end": v(140.88, -44.6) * mm});
            skLineSegment(sketch, "E407", {"start": v(141.16, -44.23) * mm, "end": v(141.4, -43.86) * mm});
            skLineSegment(sketch, "E408", {"start": v(141.8, -42.27) * mm, "end": v(142.62, -42.31) * mm});
            skLineSegment(sketch, "E409", {"start": v(142.62, -42.31) * mm, "end": v(142.62, -42.31) * mm});
            skLineSegment(sketch, "E410", {"start": v(142.62, -42.31) * mm, "end": v(143.44, -42.27) * mm});
            skLineSegment(sketch, "E411", {"start": v(143.44, -42.27) * mm, "end": v(143.52, -43.09) * mm});
            skLineSegment(sketch, "E412", {"start": v(143.52, -43.09) * mm, "end": v(143.64, -43.48) * mm});
            skLineSegment(sketch, "E413", {"start": v(143.64, -43.48) * mm, "end": v(143.83, -43.86) * mm});
            skLineSegment(sketch, "E414", {"start": v(143.83, -43.86) * mm, "end": v(144.07, -44.23) * mm});
            skLineSegment(sketch, "E415", {"start": v(144.07, -44.23) * mm, "end": v(144.36, -44.6) * mm});
            skLineSegment(sketch, "E416", {"start": v(144.36, -44.6) * mm, "end": v(144.69, -44.95) * mm});
            skLineSegment(sketch, "E417", {"start": v(144.69, -44.95) * mm, "end": v(145.58, -44.75) * mm});
            skLineSegment(sketch, "E418", {"start": v(145.58, -44.75) * mm, "end": v(145.72, -44.29) * mm});
            skLineSegment(sketch, "E419", {"start": v(145.72, -44.29) * mm, "end": v(145.82, -43.84) * mm});
            skLineSegment(sketch, "E420", {"start": v(145.82, -43.84) * mm, "end": v(145.88, -43.4) * mm});
            skLineSegment(sketch, "E421", {"start": v(145.88, -43.4) * mm, "end": v(145.88, -42.97) * mm});
            skLineSegment(sketch, "E422", {"start": v(145.88, -42.97) * mm, "end": v(145.82, -42.56) * mm});
            skLineSegment(sketch, "E423", {"start": v(145.82, -42.56) * mm, "end": v(145.54, -41.8) * mm});
            skLineSegment(sketch, "E424", {"start": v(145.54, -41.8) * mm, "end": v(146.3, -41.47) * mm});
            skLineSegment(sketch, "E425", {"start": v(146.3, -41.47) * mm, "end": v(146.3, -41.47) * mm});
            skLineSegment(sketch, "E426", {"start": v(146.3, -41.47) * mm, "end": v(147.03, -41.08) * mm});
            skLineSegment(sketch, "E427", {"start": v(147.03, -41.08) * mm, "end": v(147.45, -41.78) * mm});
            skLineSegment(sketch, "E428", {"start": v(147.45, -41.78) * mm, "end": v(147.73, -42.08) * mm});
            skLineSegment(sketch, "E429", {"start": v(147.73, -42.08) * mm, "end": v(148.07, -42.34) * mm});
            skLineSegment(sketch, "E430", {"start": v(148.07, -42.34) * mm, "end": v(148.45, -42.57) * mm});
            skLineSegment(sketch, "E431", {"start": v(148.45, -42.57) * mm, "end": v(148.86, -42.78) * mm});
            skLineSegment(sketch, "E432", {"start": v(148.86, -42.78) * mm, "end": v(149.3, -42.95) * mm});
            skLineSegment(sketch, "E433", {"start": v(149.3, -42.95) * mm, "end": v(150.02, -42.38) * mm});
            skLineSegment(sketch, "E434", {"start": v(150.02, -42.38) * mm, "end": v(149.95, -41.9) * mm});
            skLineSegment(sketch, "E435", {"start": v(149.95, -41.9) * mm, "end": v(149.85, -41.45) * mm});
            skLineSegment(sketch, "E436", {"start": v(149.85, -41.45) * mm, "end": v(149.7, -41.03) * mm});
            skLineSegment(sketch, "E437", {"start": v(149.7, -41.03) * mm, "end": v(149.53, -40.64) * mm});
            skLineSegment(sketch, "E438", {"start": v(149.53, -40.64) * mm, "end": v(149.3, -40.3) * mm});
            skLineSegment(sketch, "E439", {"start": v(149.3, -40.3) * mm, "end": v(148.7, -39.74) * mm});
            skLineSegment(sketch, "E440", {"start": v(148.7, -39.74) * mm, "end": v(149.25, -39.12) * mm});
            skLineSegment(sketch, "E441", {"start": v(149.25, -39.12) * mm, "end": v(149.25, -39.12) * mm});
            skLineSegment(sketch, "E442", {"start": v(149.25, -39.12) * mm, "end": v(149.73, -38.45) * mm});
            skLineSegment(sketch, "E443", {"start": v(149.73, -38.45) * mm, "end": v(150.42, -38.9) * mm});
            skLineSegment(sketch, "E444", {"start": v(150.42, -38.9) * mm, "end": v(150.8, -39.04) * mm});
            skLineSegment(sketch, "E445", {"start": v(150.8, -39.04) * mm, "end": v(151.22, -39.13) * mm});
            skLineSegment(sketch, "E446", {"start": v(151.22, -39.13) * mm, "end": v(151.66, -39.18) * mm});
            skLineSegment(sketch, "E447", {"start": v(151.66, -39.18) * mm, "end": v(152.13, -39.18) * mm});
            skLineSegment(sketch, "E448", {"start": v(152.13, -39.18) * mm, "end": v(152.6, -39.14) * mm});
            skLineSegment(sketch, "E449", {"start": v(152.6, -39.14) * mm, "end": v(153, -38.32) * mm});
            skLineSegment(sketch, "E450", {"start": v(153, -38.32) * mm, "end": v(152.73, -37.92) * mm});
            skLineSegment(sketch, "E451", {"start": v(152.73, -37.92) * mm, "end": v(152.44, -37.56) * mm});
            skLineSegment(sketch, "E452", {"start": v(152.44, -37.56) * mm, "end": v(152.13, -37.24) * mm});
            skLineSegment(sketch, "E453", {"start": v(152.13, -37.24) * mm, "end": v(151.8, -36.97) * mm});
            skLineSegment(sketch, "E454", {"start": v(151.8, -36.97) * mm, "end": v(151.44, -36.77) * mm});
            skLineSegment(sketch, "E455", {"start": v(151.44, -36.77) * mm, "end": v(150.67, -36.5) * mm});
            skLineSegment(sketch, "E456", {"start": v(150.67, -36.5) * mm, "end": v(150.9, -35.71) * mm});
            skLineSegment(sketch, "E457", {"start": v(150.9, -35.71) * mm, "end": v(150.9, -35.72) * mm});
            skLineSegment(sketch, "E458", {"start": v(134.62, -28.68) * mm, "end": v(134.62, -13.9) * mm});
            skLineSegment(sketch, "E459", {"start": v(132.62, 26.17) * mm, "end": v(132.62, 41.17) * mm});
            skLineSegment(sketch, "E460", {"start": v(132.62, 41.17) * mm, "end": v(135.55, 41.17) * mm});
            skLineSegment(sketch, "E461", {"start": v(152.62, -34.89) * mm, "end": v(152.62, 24.1) * mm});
            skArc(sketch, "E462", {"start": v(152.62, 24.1) * mm, "mid": v(152.24, 26.02) * mm, "end": v(151.15, 27.64) * mm});
            skLineSegment(sketch, "E463", {"start": v(139.08, 39.7) * mm, "end": v(151.15, 27.64) * mm});
            skArc(sketch, "E464", {"start": v(139.08, 39.7) * mm, "mid": v(137.46, 40.8) * mm, "end": v(135.55, 41.17) * mm});
            skLineSegment(sketch, "E465", {"start": v(132.62, 26.17) * mm, "end": v(141.15, 17.64) * mm});
            skArc(sketch, "E466", {"start": v(142.62, 14.1) * mm, "mid": v(142.24, 16.02) * mm, "end": v(141.15, 17.64) * mm});
            skLineSegment(sketch, "E467", {"start": v(142.62, 14.1) * mm, "end": v(142.62, -1.76) * mm});
            skArc(sketch, "E468", {"start": v(141.15, -5.3) * mm, "mid": v(142.24, -3.67) * mm, "end": v(142.62, -1.76) * mm});
            skLineSegment(sketch, "E469", {"start": v(141.15, -5.3) * mm, "end": v(136.08, -10.36) * mm});
            skArc(sketch, "E470", {"start": v(136.08, -10.36) * mm, "mid": v(135, -11.98) * mm, "end": v(134.62, -13.9) * mm});
            skLineSegment(sketch, "E471", {"start": v(134.62, -28.68) * mm, "end": v(134.44, -28.6) * mm});
            skLineSegment(sketch, "E472", {"start": v(134.44, -28.6) * mm, "end": v(134.02, -28.52) * mm});
            skLineSegment(sketch, "E473", {"start": v(134.02, -28.52) * mm, "end": v(133.57, -28.48) * mm});
            skLineSegment(sketch, "E474", {"start": v(133.57, -28.48) * mm, "end": v(133.11, -28.47) * mm});
            skLineSegment(sketch, "E475", {"start": v(133.11, -28.47) * mm, "end": v(132.63, -28.51) * mm});
            skLineSegment(sketch, "E476", {"start": v(132.63, -28.51) * mm, "end": v(132.24, -29.33) * mm});
            skLineSegment(sketch, "E477", {"start": v(132.24, -29.33) * mm, "end": v(132.5, -29.73) * mm});
            skLineSegment(sketch, "E478", {"start": v(132.5, -29.73) * mm, "end": v(132.8, -30.1) * mm});
            skLineSegment(sketch, "E479", {"start": v(132.8, -30.1) * mm, "end": v(133.1, -30.41) * mm});
            skLineSegment(sketch, "E480", {"start": v(133.1, -30.41) * mm, "end": v(133.44, -30.68) * mm});
            skLineSegment(sketch, "E481", {"start": v(133.44, -30.68) * mm, "end": v(133.8, -30.89) * mm});
            skLineSegment(sketch, "E482", {"start": v(133.8, -30.89) * mm, "end": v(134.57, -31.14) * mm});
            skLineSegment(sketch, "E483", {"start": v(134.57, -31.14) * mm, "end": v(134.35, -31.94) * mm});
            skLineSegment(sketch, "E484", {"start": v(134.35, -31.94) * mm, "end": v(134.35, -31.94) * mm});
            skLineSegment(sketch, "E485", {"start": v(134.35, -31.94) * mm, "end": v(134.2, -32.75) * mm});
            skLineSegment(sketch, "E486", {"start": v(134.2, -32.75) * mm, "end": v(133.4, -32.65) * mm});
            skLineSegment(sketch, "E487", {"start": v(133.4, -32.65) * mm, "end": v(132.98, -32.68) * mm});
            skLineSegment(sketch, "E488", {"start": v(132.98, -32.68) * mm, "end": v(132.57, -32.78) * mm});
            skLineSegment(sketch, "E489", {"start": v(132.57, -32.78) * mm, "end": v(132.15, -32.93) * mm});
            skLineSegment(sketch, "E490", {"start": v(132.15, -32.93) * mm, "end": v(131.73, -33.13) * mm});
            skLineSegment(sketch, "E491", {"start": v(131.73, -33.13) * mm, "end": v(131.31, -33.37) * mm});
            skLineSegment(sketch, "E492", {"start": v(131.31, -34.28) * mm, "end": v(131.73, -34.52) * mm});
            skLineSegment(sketch, "E493", {"start": v(131.73, -34.52) * mm, "end": v(132.15, -34.72) * mm});
            skLineSegment(sketch, "E494", {"start": v(132.15, -34.72) * mm, "end": v(132.57, -34.88) * mm});
            skLineSegment(sketch, "E495", {"start": v(132.57, -34.88) * mm, "end": v(132.98, -34.98) * mm});
            skLineSegment(sketch, "E496", {"start": v(133.4, -35) * mm, "end": v(134.2, -34.9) * mm});
            skLineSegment(sketch, "E497", {"start": v(134.35, -35.72) * mm, "end": v(134.35, -35.71) * mm});
            skLineSegment(sketch, "E498", {"start": v(134.35, -35.71) * mm, "end": v(134.57, -36.5) * mm});
            skLineSegment(sketch, "E499", {"start": v(134.57, -36.5) * mm, "end": v(133.8, -36.77) * mm});
            skLineSegment(sketch, "E500", {"start": v(133.44, -36.97) * mm, "end": v(133.1, -37.24) * mm});
            skLineSegment(sketch, "E501", {"start": v(133.1, -37.24) * mm, "end": v(132.8, -37.56) * mm});
            skLineSegment(sketch, "E502", {"start": v(132.5, -37.92) * mm, "end": v(132.24, -38.32) * mm});
            skLineSegment(sketch, "E503", {"start": v(132.24, -38.32) * mm, "end": v(132.63, -39.14) * mm});
            skLineSegment(sketch, "E504", {"start": v(132.63, -39.14) * mm, "end": v(133.11, -39.18) * mm});
            skLineSegment(sketch, "E505", {"start": v(133.11, -39.18) * mm, "end": v(133.57, -39.18) * mm});
            skLineSegment(sketch, "E506", {"start": v(135.98, -39.12) * mm, "end": v(136.53, -39.74) * mm});
            skLineSegment(sketch, "E507", {"start": v(135.94, -40.3) * mm, "end": v(135.71, -40.64) * mm});
            skLineSegment(sketch, "E508", {"start": v(135.71, -40.64) * mm, "end": v(135.53, -41.03) * mm});
            skLineSegment(sketch, "E509", {"start": v(135.53, -41.03) * mm, "end": v(135.39, -41.45) * mm});
            skLineSegment(sketch, "E510", {"start": v(135.39, -41.45) * mm, "end": v(135.28, -41.9) * mm});
            skLineSegment(sketch, "E511", {"start": v(136.37, -42.78) * mm, "end": v(136.8, -42.57) * mm});
            skLineSegment(sketch, "E512", {"start": v(137.5, -42.08) * mm, "end": v(137.79, -41.78) * mm});
            skLineSegment(sketch, "E513", {"start": v(138.94, -41.47) * mm, "end": v(139.7, -41.8) * mm});
            skLineSegment(sketch, "E514", {"start": v(139.42, -42.56) * mm, "end": v(139.35, -42.97) * mm});
            skLineSegment(sketch, "E515", {"start": v(139.35, -42.97) * mm, "end": v(139.36, -43.4) * mm});
            skLineSegment(sketch, "E516", {"start": v(139.36, -43.4) * mm, "end": v(139.41, -43.84) * mm});
            skLineSegment(sketch, "E517", {"start": v(139.41, -43.84) * mm, "end": v(139.51, -44.29) * mm});
            skLineSegment(sketch, "E518", {"start": v(139.66, -44.75) * mm, "end": v(140.55, -44.95) * mm});
            skLineSegment(sketch, "E519", {"start": v(140.88, -44.6) * mm, "end": v(141.16, -44.23) * mm});
            skLineSegment(sketch, "E520", {"start": v(141.4, -43.86) * mm, "end": v(141.6, -43.48) * mm});
            skLineSegment(sketch, "E521", {"start": v(141.6, -43.48) * mm, "end": v(141.71, -43.09) * mm});
            skLineSegment(sketch, "E522", {"start": v(141.71, -43.09) * mm, "end": v(141.8, -42.27) * mm});
            skLineSegment(sketch, "E523", {"start": v(131.31, -33.37) * mm, "end": v(131.31, -34.28) * mm});
            skCircle(sketch, "E524", {"center": v(142.62, -33.83) * mm, "radius": 0.75 * mm});
            skCircle(sketch, "E525", {"center": v(98.97, -34.17) * mm, "radius": 2.22 * mm});
            skCircle(sketch, "E526", {"center": v(98.97, -26.05) * mm, "radius": 0.55 * mm});
            skPoint(sketch, "E527.endSnap0", {"position": v(-2, -18.52) * mm});
            skLineSegment(sketch, "E528", {"start": v(-2, -15.8) * mm, "end": v(-0.05, -15.8) * mm});
            skLineSegment(sketch, "E529", {"start": v(27.56, -15.7) * mm, "end": v(27.56, -5.9) * mm});
            skLineSegment(sketch, "E530", {"start": v(-0.05, -15.8) * mm, "end": v(-0.05, -6) * mm});
            skLineSegment(sketch, "E531.trimOffspring", {"start": v(27.56, -15.7) * mm, "end": v(29.5, -15.7) * mm});
            skPoint(sketch, "E532.orphan", {"position": v(-2, -10.02) * mm});
            skLineSegment(sketch, "E533", {"start": v(-0.05, 23) * mm, "end": v(-0.05, 30) * mm});
            skLineSegment(sketch, "E534", {"start": v(27.56, 23.1) * mm, "end": v(27.56, 30.1) * mm});
            skArc(sketch, "E535", {"start": v(47.5, 10.1) * mm, "mid": v(41.67, 24.23) * mm, "end": v(27.56, 30.1) * mm});
            skPoint(sketch, "E536.endSnap0", {"position": v(-0.05, 10) * mm});
            skLineSegment(sketch, "E537", {"start": v(-20, 10) * mm, "end": v(-20, -33.15) * mm});
            skArc(sketch, "E538.trimOffspring", {"start": v(-0.05, 30) * mm, "mid": v(-14.16, 24.12) * mm, "end": v(-20, 10) * mm});
            skArc(sketch, "E539.trimOffspring", {"start": v(35.52, 2.57) * mm, "mid": v(38.42, 11.48) * mm, "end": v(33.4, 19.4) * mm});
            skLineSegment(sketch, "E540", {"start": v(27.56, -5.9) * mm, "end": v(35.52, 2.57) * mm});
            skLineSegment(sketch, "E541", {"start": v(27.56, 23.1) * mm, "end": v(33.4, 19.4) * mm});
            skArc(sketch, "E542", {"start": v(37.03, 0.54) * mm, "mid": v(40.93, 11.55) * mm, "end": v(34.79, 21.48) * mm});
            skLineSegment(sketch, "E543.MirrorCS", {"start": v(-0.05, -9) * mm, "end": v(-9.52, 0.43) * mm});
            skLineSegment(sketch, "E544", {"start": v(27.56, 26.1) * mm, "end": v(34.79, 21.48) * mm});
            skLineSegment(sketch, "E545", {"start": v(37.03, 0.54) * mm, "end": v(27.56, -9) * mm});
            skLineSegment(sketch, "E546", {"start": v(-0.05, -6) * mm, "end": v(-0.05, 23) * mm});
            skLineSegment(sketch, "E547", {"start": v(27.56, 23.1) * mm, "end": v(27.56, -9) * mm});
            skLineSegment(sketch, "E548", {"start": v(-129.43, -31.07) * mm, "end": v(-129.43, -28.07) * mm});
            skLineSegment(sketch, "E549", {"start": v(-129.43, 0.93) * mm, "end": v(-129.43, 3.93) * mm});
            skArc(sketch, "E550", {"start": v(-92.35, -21.53) * mm, "mid": v(-88.45, -10.52) * mm, "end": v(-94.6, -0.6) * mm});
            skLineSegment(sketch, "E551.MirrorCS", {"start": v(-129.43, -31.07) * mm, "end": v(-138.9, -21.63) * mm});
            skLineSegment(sketch, "E552", {"start": v(-101.82, 4.04) * mm, "end": v(-94.6, -0.6) * mm});
            skArc(sketch, "E553.trimOffspring", {"start": v(-136.66, -0.7) * mm, "mid": v(-142.8, -10.63) * mm, "end": v(-138.9, -21.63) * mm});
            skLineSegment(sketch, "E554.MirrorCS", {"start": v(-129.43, 3.93) * mm, "end": v(-136.66, -0.7) * mm});
            skLineSegment(sketch, "E555", {"start": v(-92.35, -21.53) * mm, "end": v(-101.82, -31.06) * mm});
            skLineSegment(sketch, "E556", {"start": v(-129.43, -28.07) * mm, "end": v(-129.43, 0.93) * mm});
            skLineSegment(sketch, "E557", {"start": v(-101.82, 1.04) * mm, "end": v(-101.82, -31.06) * mm});
            skLineSegment(sketch, "E558", {"start": v(-101.82, 4.04) * mm, "end": v(-101.82, 1.04) * mm});
            skLineSegment(sketch, "E559", {"start": v(-20, 0) * mm, "end": v(-12.1, 15.98) * mm});
            skLineSegment(sketch, "E560", {"start": v(47.5, 10.1) * mm, "end": v(39.85, 15.58) * mm});
            skLineSegment(sketch, "E561", {"start": v(-10, -19.95) * mm, "end": v(-10, -29.95) * mm});
            skLineSegment(sketch, "E562.0", {"start": v(0.68, -5.31) * mm, "end": v(-7.28, 3.15) * mm});
            skArc(sketch, "E562.1", {"start": v(-5.36, 18.44) * mm, "mid": v(-9.92, 11.25) * mm, "end": v(-7.28, 3.15) * mm});
            skLineSegment(sketch, "E562.2", {"start": v(0.49, 22.16) * mm, "end": v(-5.36, 18.44) * mm});
            skLineSegment(sketch, "E563.0", {"start": v(26.83, -5.2) * mm, "end": v(34.8, 3.26) * mm});
            skArc(sketch, "E563.1", {"start": v(34.8, 3.26) * mm, "mid": v(37.43, 11.35) * mm, "end": v(32.87, 18.55) * mm});
            skLineSegment(sketch, "E563.2", {"start": v(27.02, 22.26) * mm, "end": v(32.87, 18.55) * mm});
            skLineSegment(sketch, "E564.0", {"start": v(0.66, -8.3) * mm, "end": v(-8.82, 1.14) * mm});
            skArc(sketch, "E564.1", {"start": v(-6.74, 20.53) * mm, "mid": v(-12.43, 11.33) * mm, "end": v(-8.82, 1.14) * mm});
            skLineSegment(sketch, "E564.2", {"start": v(0.49, 25.16) * mm, "end": v(-6.74, 20.53) * mm});
            skLineSegment(sketch, "E565", {"start": v(-12.1, 15.98) * mm, "end": v(-10.12, 17.33) * mm});
            skLineSegment(sketch, "E566", {"start": v(-0.05, 21.82) * mm, "end": v(-6.74, 20.53) * mm});
            skLineSegment(sketch, "E567", {"start": v(-0.05, -4.54) * mm, "end": v(-7, -0.68) * mm});
            skLineSegment(sketch, "E568", {"start": v(-12.5, 10) * mm, "end": v(-27.5, 10) * mm});
            skLineSegment(sketch, "E569", {"start": v(-27.5, 10) * mm, "end": v(-27.5, 20.53) * mm});
            skLineSegment(sketch, "E570", {"start": v(-27.5, 20.53) * mm, "end": v(-6.74, 20.53) * mm});
            skLineSegment(sketch, "E571", {"start": v(-27.5, 10) * mm, "end": v(-27.5, -0.68) * mm});
            skLineSegment(sketch, "E572", {"start": v(-27.5, -0.68) * mm, "end": v(-7, -0.68) * mm});
            skLineSegment(sketch, "E573", {"start": v(-27.5, 20.53) * mm, "end": v(-27.5, 21.13) * mm});
            skLineSegment(sketch, "E574", {"start": v(-27.5, 21.13) * mm, "end": v(-5.8, 21.13) * mm});
            skLineSegment(sketch, "E575", {"start": v(-27.5, -0.68) * mm, "end": v(-27.5, -1.28) * mm});
            skLineSegment(sketch, "E576", {"start": v(-27.5, -1.28) * mm, "end": v(-6.4, -1.28) * mm});
            skSolve(sketch);
        }
        {
            var Q0;
            Q0=makeQuery(id+"F0.imprint","IMPRINT",FACE,{"disambiguationData":[TD([[makeQuery(id+"F0.imprint","IMPRINT",EDGE,{"derivedFrom":sQuery(id+"F0.wireOp",EDGE,"E0")}),1.0]])]});
            var Q1;
            Q1=makeQuery(id+"F0.imprint","IMPRINT",FACE,{"disambiguationData":[TD([[makeQuery(id+"F0.imprint","IMPRINT",EDGE,{"derivedFrom":sQuery(id+"F0.wireOp",EDGE,"E117")}),1.0]])]});
            var Q2;
            {var subQ5=sQuery(id+"F0.wireOp",EDGE,"E543.MirrorCS");Q2=makeQuery(id+"F0.imprint","IMPRINT",FACE,{"disambiguationData":[TD([[makeQuery(id+"F0.imprint","IMPRINT",EDGE,{"derivedFrom":subQ5}),-1.0]])]});}
            var Q3;
            {var subQ7=sQuery(id+"F0.wireOp",EDGE,"E559");var subQ8=sQuery(id+"F0.wireOp",EDGE,"E537");var subQ9=makeQuery(id+"F0.imprint","INTERSECT",VERTEX,{"derivedFrom":[subQ8,subQ7]});Q3=makeQuery(id+"F0.imprint","IMPRINT",FACE,{"disambiguationData":[TD([[makeQuery(id+"F0.imprint","IMPRINT",EDGE,{"disambiguationData":[TD([[subQ9,-1.0]])],"derivedFrom":subQ8}),1.0]])]});}
            var Q4;
            {var subQ0=sQuery(id+"F0.wireOp",EDGE,"E565");Q4=makeQuery(id+"F0.imprint","IMPRINT",FACE,{"disambiguationData":[TD([[makeQuery(id+"F0.imprint","IMPRINT",EDGE,{"derivedFrom":subQ0}),-1.0]])]});}
            var Q5;
            {var subQ0=sQuery(id+"F0.wireOp",EDGE,"E576");var subQ1=sQuery(id+"F0.wireOp",EDGE,"E537");var subQ2=makeQuery(id+"F0.imprint","INTERSECT",VERTEX,{"derivedFrom":[subQ1,subQ0]});Q5=makeQuery(id+"F0.imprint","IMPRINT",FACE,{"disambiguationData":[TD([[makeQuery(id+"F0.imprint","IMPRINT",EDGE,{"disambiguationData":[TD([[subQ2,1.0]])],"derivedFrom":subQ1}),1.0]])]});}
            extrude(context, id + "F1", {"entities" : qUnion([Q0, Q1, Q2, Q3, Q4, Q5]), "endBound" : BoundingType.SYMMETRIC, "depth" : 3 * mm});
        }
        {
            var Q0;
            {var subQ12=sQuery(id+"F0.wireOp",EDGE,"E562.1");Q0=makeQuery(id+"F0.imprint","IMPRINT",FACE,{"disambiguationData":[TD([[makeQuery(id+"F0.imprint","IMPRINT",EDGE,{"derivedFrom":subQ12}),-1.0]])]});}
            var Q1;
            Q1=makeQuery(id+"F0.imprint","IMPRINT",FACE,{"disambiguationData":[TD([[makeQuery(id+"F0.imprint","IMPRINT",EDGE,{"derivedFrom":sQuery(id+"F0.wireOp",EDGE,"E539.trimOffspring")}),1.0]])]});
            var Q2;
            Q2=makeQuery(id+"F0.imprint","IMPRINT",FACE,{"disambiguationData":[TD([[makeQuery(id+"F0.imprint","IMPRINT",EDGE,{"derivedFrom":sQuery(id+"F0.wireOp",EDGE,"E539.trimOffspring")}),-1.0]])]});
            var Q3;
            {var subQ5=sQuery(id+"F0.wireOp",EDGE,"E566");Q3=makeQuery(id+"F0.imprint","IMPRINT",FACE,{"disambiguationData":[TD([[makeQuery(id+"F0.imprint","IMPRINT",EDGE,{"derivedFrom":subQ5}),-1.0]])]});}
            var Q4;
            {var subQ5=sQuery(id+"F0.wireOp",EDGE,"E567");Q4=makeQuery(id+"F0.imprint","IMPRINT",FACE,{"disambiguationData":[TD([[makeQuery(id+"F0.imprint","IMPRINT",EDGE,{"derivedFrom":subQ5}),1.0]])]});}
            var Q5;
            {var subQ5=sQuery(id+"F0.wireOp",EDGE,"E562.1");Q5=makeQuery(id+"F0.imprint","IMPRINT",FACE,{"disambiguationData":[TD([[makeQuery(id+"F0.imprint","IMPRINT",EDGE,{"derivedFrom":subQ5}),1.0]])]});}
            var Q6;
            {var subQ5=sQuery(id+"F0.wireOp",EDGE,"E563.1");Q6=makeQuery(id+"F0.imprint","IMPRINT",FACE,{"disambiguationData":[TD([[makeQuery(id+"F0.imprint","IMPRINT",EDGE,{"derivedFrom":subQ5}),1.0]])]});}
            var Q7;
            {var subQ0=sQuery(id+"F0.wireOp",EDGE,"E565");Q7=makeQuery(id+"F0.imprint","IMPRINT",FACE,{"disambiguationData":[TD([[makeQuery(id+"F0.imprint","IMPRINT",EDGE,{"derivedFrom":subQ0}),1.0]])]});}
            var Q8;
            {var subQ5=sQuery(id+"F0.wireOp",EDGE,"E569");Q8=makeQuery(id+"F0.imprint","IMPRINT",FACE,{"disambiguationData":[TD([[makeQuery(id+"F0.imprint","IMPRINT",EDGE,{"derivedFrom":subQ5}),-1.0]])]});}
            var Q9;
            {var subQ3=sQuery(id+"F0.wireOp",EDGE,"E571");Q9=makeQuery(id+"F0.imprint","IMPRINT",FACE,{"disambiguationData":[TD([[makeQuery(id+"F0.imprint","IMPRINT",EDGE,{"derivedFrom":subQ3}),1.0]])]});}
            var Q10;
            {var subQ1=sQuery(id+"F0.wireOp",EDGE,"E537");var subQ3=sQuery(id+"F0.wireOp",EDGE,"E559");var subQ4=makeQuery(id+"F0.imprint","INTERSECT",VERTEX,{"derivedFrom":[subQ1,subQ3]});Q10=makeQuery(id+"F0.imprint","IMPRINT",FACE,{"disambiguationData":[TD([[makeQuery(id+"F0.imprint","IMPRINT",EDGE,{"disambiguationData":[TD([[subQ4,-1.0]])],"derivedFrom":subQ3}),1.0]])]});}
            var Q11;
            {var subQ7=sQuery(id+"F0.wireOp",EDGE,"E559");var subQ8=sQuery(id+"F0.wireOp",EDGE,"E537");var subQ9=makeQuery(id+"F0.imprint","INTERSECT",VERTEX,{"derivedFrom":[subQ8,subQ7]});Q11=makeQuery(id+"F0.imprint","IMPRINT",FACE,{"disambiguationData":[TD([[makeQuery(id+"F0.imprint","IMPRINT",EDGE,{"disambiguationData":[TD([[subQ9,-1.0]])],"derivedFrom":subQ8}),1.0]])]});}
            var Q12;
            {var subQ0=sQuery(id+"F0.wireOp",EDGE,"E565");Q12=makeQuery(id+"F0.imprint","IMPRINT",FACE,{"disambiguationData":[TD([[makeQuery(id+"F0.imprint","IMPRINT",EDGE,{"derivedFrom":subQ0}),-1.0]])]});}
            var Q13;
            {var subQ0=sQuery(id+"F0.wireOp",EDGE,"E574");var subQ1=sQuery(id+"F0.wireOp",EDGE,"E538.trimOffspring");var subQ2=makeQuery(id+"F0.imprint","INTERSECT",VERTEX,{"derivedFrom":[subQ1,subQ0]});Q13=makeQuery(id+"F0.imprint","IMPRINT",FACE,{"disambiguationData":[TD([[makeQuery(id+"F0.imprint","IMPRINT",EDGE,{"disambiguationData":[TD([[subQ2,-1.0]])],"derivedFrom":subQ1}),1.0]])]});}
            var Q14;
            {var subQ5=sQuery(id+"F0.wireOp",EDGE,"E573");Q14=makeQuery(id+"F0.imprint","IMPRINT",FACE,{"disambiguationData":[TD([[makeQuery(id+"F0.imprint","IMPRINT",EDGE,{"derivedFrom":subQ5}),-1.0]])]});}
            var Q15;
            {var subQ0=sQuery(id+"F0.wireOp",EDGE,"E572");var subQ1=sQuery(id+"F0.wireOp",EDGE,"E543.MirrorCS");var subQ2=makeQuery(id+"F0.imprint","INTERSECT",VERTEX,{"derivedFrom":[subQ1,subQ0]});Q15=makeQuery(id+"F0.imprint","IMPRINT",FACE,{"disambiguationData":[TD([[makeQuery(id+"F0.imprint","IMPRINT",EDGE,{"disambiguationData":[TD([[subQ2,1.0]])],"derivedFrom":subQ1}),-1.0]])]});}
            var Q16;
            {var subQ0=sQuery(id+"F0.wireOp",EDGE,"E576");var subQ1=sQuery(id+"F0.wireOp",EDGE,"E537");var subQ2=makeQuery(id+"F0.imprint","INTERSECT",VERTEX,{"derivedFrom":[subQ1,subQ0]});Q16=makeQuery(id+"F0.imprint","IMPRINT",FACE,{"disambiguationData":[TD([[makeQuery(id+"F0.imprint","IMPRINT",EDGE,{"disambiguationData":[TD([[subQ2,1.0]])],"derivedFrom":subQ1}),1.0]])]});}
            var Q17;
            {var subQ5=sQuery(id+"F0.wireOp",EDGE,"E575");Q17=makeQuery(id+"F0.imprint","IMPRINT",FACE,{"disambiguationData":[TD([[makeQuery(id+"F0.imprint","IMPRINT",EDGE,{"derivedFrom":subQ5}),1.0]])]});}
            extrude(context, id + "F2", {"entities" : qUnion([Q0, Q1, Q2, Q3, Q4, Q5, Q6, Q7, Q8, Q9, Q10, Q11, Q12, Q13, Q14, Q15, Q16, Q17]), "depth" : 20 * mm});
        }
        {
            var Q0;
            {var subQ12=sQuery(id+"F0.wireOp",EDGE,"E562.1");Q0=makeQuery(id+"F0.imprint","IMPRINT",FACE,{"disambiguationData":[TD([[makeQuery(id+"F0.imprint","IMPRINT",EDGE,{"derivedFrom":subQ12}),-1.0]])]});}
            var Q1;
            Q1=makeQuery(id+"F0.imprint","IMPRINT",FACE,{"disambiguationData":[TD([[makeQuery(id+"F0.imprint","IMPRINT",EDGE,{"derivedFrom":sQuery(id+"F0.wireOp",EDGE,"E539.trimOffspring")}),1.0]])]});
            var Q2;
            Q2=makeQuery(id+"F0.imprint","IMPRINT",FACE,{"disambiguationData":[TD([[makeQuery(id+"F0.imprint","IMPRINT",EDGE,{"derivedFrom":sQuery(id+"F0.wireOp",EDGE,"E539.trimOffspring")}),-1.0]])]});
            var Q3;
            {var subQ5=sQuery(id+"F0.wireOp",EDGE,"E567");Q3=makeQuery(id+"F0.imprint","IMPRINT",FACE,{"disambiguationData":[TD([[makeQuery(id+"F0.imprint","IMPRINT",EDGE,{"derivedFrom":subQ5}),1.0]])]});}
            var Q4;
            {var subQ5=sQuery(id+"F0.wireOp",EDGE,"E566");Q4=makeQuery(id+"F0.imprint","IMPRINT",FACE,{"disambiguationData":[TD([[makeQuery(id+"F0.imprint","IMPRINT",EDGE,{"derivedFrom":subQ5}),-1.0]])]});}
            extrude(context, id + "F3", {"entities" : qUnion([Q0, Q1, Q2, Q3, Q4]), "operationType" : NewBodyOperationType.ADD, "oppositeDirection" : true, "depth" : 60 * mm});
        }
        {
            var Q0;
            {var subQ5=sQuery(id+"F0.wireOp",EDGE,"E562.1");Q0=makeQuery(id+"F0.imprint","IMPRINT",FACE,{"disambiguationData":[TD([[makeQuery(id+"F0.imprint","IMPRINT",EDGE,{"derivedFrom":subQ5}),-1.0]])]});}
            var Q1;
            {var subQ5=sQuery(id+"F0.wireOp",EDGE,"E562.1");Q1=makeQuery(id+"F0.imprint","IMPRINT",FACE,{"disambiguationData":[TD([[makeQuery(id+"F0.imprint","IMPRINT",EDGE,{"derivedFrom":subQ5}),1.0]])]});}
            var Q2;
            {var subQ5=sQuery(id+"F0.wireOp",EDGE,"E563.1");Q2=makeQuery(id+"F0.imprint","IMPRINT",FACE,{"disambiguationData":[TD([[makeQuery(id+"F0.imprint","IMPRINT",EDGE,{"derivedFrom":subQ5}),1.0]])]});}
            var Q3;
            {var subQ3=sQuery(id+"F0.wireOp",EDGE,"E571");Q3=makeQuery(id+"F0.imprint","IMPRINT",FACE,{"disambiguationData":[TD([[makeQuery(id+"F0.imprint","IMPRINT",EDGE,{"derivedFrom":subQ3}),1.0]])]});}
            var Q4;
            {var subQ1=sQuery(id+"F0.wireOp",EDGE,"E537");var subQ3=sQuery(id+"F0.wireOp",EDGE,"E559");var subQ4=makeQuery(id+"F0.imprint","INTERSECT",VERTEX,{"derivedFrom":[subQ1,subQ3]});Q4=makeQuery(id+"F0.imprint","IMPRINT",FACE,{"disambiguationData":[TD([[makeQuery(id+"F0.imprint","IMPRINT",EDGE,{"disambiguationData":[TD([[subQ4,-1.0]])],"derivedFrom":subQ3}),1.0]])]});}
            var Q5;
            {var subQ7=sQuery(id+"F0.wireOp",EDGE,"E559");var subQ8=sQuery(id+"F0.wireOp",EDGE,"E537");var subQ9=makeQuery(id+"F0.imprint","INTERSECT",VERTEX,{"derivedFrom":[subQ8,subQ7]});Q5=makeQuery(id+"F0.imprint","IMPRINT",FACE,{"disambiguationData":[TD([[makeQuery(id+"F0.imprint","IMPRINT",EDGE,{"disambiguationData":[TD([[subQ9,-1.0]])],"derivedFrom":subQ8}),1.0]])]});}
            var Q6;
            {var subQ0=sQuery(id+"F0.wireOp",EDGE,"E565");Q6=makeQuery(id+"F0.imprint","IMPRINT",FACE,{"disambiguationData":[TD([[makeQuery(id+"F0.imprint","IMPRINT",EDGE,{"derivedFrom":subQ0}),-1.0]])]});}
            var Q7;
            {var subQ0=sQuery(id+"F0.wireOp",EDGE,"E565");Q7=makeQuery(id+"F0.imprint","IMPRINT",FACE,{"disambiguationData":[TD([[makeQuery(id+"F0.imprint","IMPRINT",EDGE,{"derivedFrom":subQ0}),1.0]])]});}
            var Q8;
            {var subQ5=sQuery(id+"F0.wireOp",EDGE,"E569");Q8=makeQuery(id+"F0.imprint","IMPRINT",FACE,{"disambiguationData":[TD([[makeQuery(id+"F0.imprint","IMPRINT",EDGE,{"derivedFrom":subQ5}),-1.0]])]});}
            var Q9;
            {var subQ0=sQuery(id+"F0.wireOp",EDGE,"E576");var subQ1=sQuery(id+"F0.wireOp",EDGE,"E537");var subQ2=makeQuery(id+"F0.imprint","INTERSECT",VERTEX,{"derivedFrom":[subQ1,subQ0]});Q9=makeQuery(id+"F0.imprint","IMPRINT",FACE,{"disambiguationData":[TD([[makeQuery(id+"F0.imprint","IMPRINT",EDGE,{"disambiguationData":[TD([[subQ2,1.0]])],"derivedFrom":subQ1}),1.0]])]});}
            var Q10;
            {var subQ0=sQuery(id+"F0.wireOp",EDGE,"E572");var subQ1=sQuery(id+"F0.wireOp",EDGE,"E543.MirrorCS");var subQ2=makeQuery(id+"F0.imprint","INTERSECT",VERTEX,{"derivedFrom":[subQ1,subQ0]});Q10=makeQuery(id+"F0.imprint","IMPRINT",FACE,{"disambiguationData":[TD([[makeQuery(id+"F0.imprint","IMPRINT",EDGE,{"disambiguationData":[TD([[subQ2,1.0]])],"derivedFrom":subQ1}),-1.0]])]});}
            var Q11;
            {var subQ0=sQuery(id+"F0.wireOp",EDGE,"E574");var subQ1=sQuery(id+"F0.wireOp",EDGE,"E538.trimOffspring");var subQ2=makeQuery(id+"F0.imprint","INTERSECT",VERTEX,{"derivedFrom":[subQ1,subQ0]});Q11=makeQuery(id+"F0.imprint","IMPRINT",FACE,{"disambiguationData":[TD([[makeQuery(id+"F0.imprint","IMPRINT",EDGE,{"disambiguationData":[TD([[subQ2,-1.0]])],"derivedFrom":subQ1}),1.0]])]});}
            var Q12;
            {var subQ5=sQuery(id+"F0.wireOp",EDGE,"E575");Q12=makeQuery(id+"F0.imprint","IMPRINT",FACE,{"disambiguationData":[TD([[makeQuery(id+"F0.imprint","IMPRINT",EDGE,{"derivedFrom":subQ5}),1.0]])]});}
            var Q13;
            {var subQ5=sQuery(id+"F0.wireOp",EDGE,"E573");Q13=makeQuery(id+"F0.imprint","IMPRINT",FACE,{"disambiguationData":[TD([[makeQuery(id+"F0.imprint","IMPRINT",EDGE,{"derivedFrom":subQ5}),-1.0]])]});}
            extrude(context, id + "F4", {"entities" : qUnion([Q0, Q1, Q2, Q3, Q4, Q5, Q6, Q7, Q8, Q9, Q10, Q11, Q12, Q13]), "operationType" : NewBodyOperationType.REMOVE, "depth" : 19 * mm});
        }
        {
            var Q0;
            {var subQ5=sQuery(id+"F0.wireOp",EDGE,"E562.1");Q0=makeQuery(id+"F0.imprint","IMPRINT",FACE,{"disambiguationData":[TD([[makeQuery(id+"F0.imprint","IMPRINT",EDGE,{"derivedFrom":subQ5}),-1.0]])]});}
            extrude(context, id + "F5", {"entities" : qUnion([Q0]), "operationType" : NewBodyOperationType.ADD, "depth" : 16.8 * mm});
        }
        {
            var Q0;
            {var subQ7=sQuery(id+"F0.wireOp",EDGE,"E559");var subQ8=sQuery(id+"F0.wireOp",EDGE,"E537");var subQ9=makeQuery(id+"F0.imprint","INTERSECT",VERTEX,{"derivedFrom":[subQ8,subQ7]});Q0=makeQuery(id+"F0.imprint","IMPRINT",FACE,{"disambiguationData":[TD([[makeQuery(id+"F0.imprint","IMPRINT",EDGE,{"disambiguationData":[TD([[subQ9,-1.0]])],"derivedFrom":subQ8}),1.0]])]});}
            var Q1;
            {var subQ1=sQuery(id+"F0.wireOp",EDGE,"E537");var subQ3=sQuery(id+"F0.wireOp",EDGE,"E559");var subQ4=makeQuery(id+"F0.imprint","INTERSECT",VERTEX,{"derivedFrom":[subQ1,subQ3]});Q1=makeQuery(id+"F0.imprint","IMPRINT",FACE,{"disambiguationData":[TD([[makeQuery(id+"F0.imprint","IMPRINT",EDGE,{"disambiguationData":[TD([[subQ4,-1.0]])],"derivedFrom":subQ3}),1.0]])]});}
            var Q2;
            {var subQ0=sQuery(id+"F0.wireOp",EDGE,"E565");Q2=makeQuery(id+"F0.imprint","IMPRINT",FACE,{"disambiguationData":[TD([[makeQuery(id+"F0.imprint","IMPRINT",EDGE,{"derivedFrom":subQ0}),1.0]])]});}
            var Q3;
            {var subQ0=sQuery(id+"F0.wireOp",EDGE,"E565");Q3=makeQuery(id+"F0.imprint","IMPRINT",FACE,{"disambiguationData":[TD([[makeQuery(id+"F0.imprint","IMPRINT",EDGE,{"derivedFrom":subQ0}),-1.0]])]});}
            extrude(context, id + "F6", {"entities" : qUnion([Q0, Q1, Q2, Q3]), "operationType" : NewBodyOperationType.ADD, "depth" : 16.8 * mm});
        }
        {
            var Q0;
            {var subQ7=sQuery(id+"F0.wireOp",EDGE,"E559");var subQ8=sQuery(id+"F0.wireOp",EDGE,"E537");var subQ9=makeQuery(id+"F0.imprint","INTERSECT",VERTEX,{"derivedFrom":[subQ8,subQ7]});Q0=makeQuery(id+"F0.imprint","IMPRINT",FACE,{"disambiguationData":[TD([[makeQuery(id+"F0.imprint","IMPRINT",EDGE,{"disambiguationData":[TD([[subQ9,-1.0]])],"derivedFrom":subQ8}),1.0]])]});}
            var Q1;
            {var subQ0=sQuery(id+"F0.wireOp",EDGE,"E565");Q1=makeQuery(id+"F0.imprint","IMPRINT",FACE,{"disambiguationData":[TD([[makeQuery(id+"F0.imprint","IMPRINT",EDGE,{"derivedFrom":subQ0}),-1.0]])]});}
            var Q2;
            {var subQ1=sQuery(id+"F0.wireOp",EDGE,"E537");var subQ3=sQuery(id+"F0.wireOp",EDGE,"E559");var subQ4=makeQuery(id+"F0.imprint","INTERSECT",VERTEX,{"derivedFrom":[subQ1,subQ3]});Q2=makeQuery(id+"F0.imprint","IMPRINT",FACE,{"disambiguationData":[TD([[makeQuery(id+"F0.imprint","IMPRINT",EDGE,{"disambiguationData":[TD([[subQ4,-1.0]])],"derivedFrom":subQ3}),1.0]])]});}
            var Q3;
            {var subQ0=sQuery(id+"F0.wireOp",EDGE,"E565");Q3=makeQuery(id+"F0.imprint","IMPRINT",FACE,{"disambiguationData":[TD([[makeQuery(id+"F0.imprint","IMPRINT",EDGE,{"derivedFrom":subQ0}),1.0]])]});}
            extrude(context, id + "F7", {"entities" : qUnion([Q0, Q1, Q2, Q3]), "operationType" : NewBodyOperationType.REMOVE, "depth" : 15.8 * mm});
        }
        {
            var Q0;
            {var subQ0=sQuery(id+"F0.wireOp",EDGE,"E572");var subQ1=sQuery(id+"F0.wireOp",EDGE,"E543.MirrorCS");var subQ2=makeQuery(id+"F0.imprint","INTERSECT",VERTEX,{"derivedFrom":[subQ1,subQ0]});Q0=makeQuery(id+"F0.imprint","IMPRINT",FACE,{"disambiguationData":[TD([[makeQuery(id+"F0.imprint","IMPRINT",EDGE,{"disambiguationData":[TD([[subQ2,1.0]])],"derivedFrom":subQ1}),-1.0]])]});}
            var Q1;
            {var subQ0=sQuery(id+"F0.wireOp",EDGE,"E576");var subQ1=sQuery(id+"F0.wireOp",EDGE,"E537");var subQ2=makeQuery(id+"F0.imprint","INTERSECT",VERTEX,{"derivedFrom":[subQ1,subQ0]});Q1=makeQuery(id+"F0.imprint","IMPRINT",FACE,{"disambiguationData":[TD([[makeQuery(id+"F0.imprint","IMPRINT",EDGE,{"disambiguationData":[TD([[subQ2,1.0]])],"derivedFrom":subQ1}),1.0]])]});}
            var Q2;
            {var subQ5=sQuery(id+"F0.wireOp",EDGE,"E575");Q2=makeQuery(id+"F0.imprint","IMPRINT",FACE,{"disambiguationData":[TD([[makeQuery(id+"F0.imprint","IMPRINT",EDGE,{"derivedFrom":subQ5}),1.0]])]});}
            var Q3;
            {var subQ0=sQuery(id+"F0.wireOp",EDGE,"E574");var subQ1=sQuery(id+"F0.wireOp",EDGE,"E538.trimOffspring");var subQ2=makeQuery(id+"F0.imprint","INTERSECT",VERTEX,{"derivedFrom":[subQ1,subQ0]});Q3=makeQuery(id+"F0.imprint","IMPRINT",FACE,{"disambiguationData":[TD([[makeQuery(id+"F0.imprint","IMPRINT",EDGE,{"disambiguationData":[TD([[subQ2,-1.0]])],"derivedFrom":subQ1}),1.0]])]});}
            var Q4;
            {var subQ5=sQuery(id+"F0.wireOp",EDGE,"E573");Q4=makeQuery(id+"F0.imprint","IMPRINT",FACE,{"disambiguationData":[TD([[makeQuery(id+"F0.imprint","IMPRINT",EDGE,{"derivedFrom":subQ5}),-1.0]])]});}
            extrude(context, id + "F8", {"entities" : qUnion([Q0, Q1, Q2, Q3, Q4]), "operationType" : NewBodyOperationType.ADD, "depth" : 19 * mm});
        }
        {
            var Q0;
            {var subQ0=sQuery(id+"F0.wireOp",EDGE,"E572");var subQ1=sQuery(id+"F0.wireOp",EDGE,"E543.MirrorCS");var subQ2=makeQuery(id+"F0.imprint","INTERSECT",VERTEX,{"derivedFrom":[subQ1,subQ0]});Q0=makeQuery(id+"F0.imprint","IMPRINT",FACE,{"disambiguationData":[TD([[makeQuery(id+"F0.imprint","IMPRINT",EDGE,{"disambiguationData":[TD([[subQ2,1.0]])],"derivedFrom":subQ1}),-1.0]])]});}
            var Q1;
            {var subQ0=sQuery(id+"F0.wireOp",EDGE,"E576");var subQ1=sQuery(id+"F0.wireOp",EDGE,"E537");var subQ2=makeQuery(id+"F0.imprint","INTERSECT",VERTEX,{"derivedFrom":[subQ1,subQ0]});Q1=makeQuery(id+"F0.imprint","IMPRINT",FACE,{"disambiguationData":[TD([[makeQuery(id+"F0.imprint","IMPRINT",EDGE,{"disambiguationData":[TD([[subQ2,1.0]])],"derivedFrom":subQ1}),1.0]])]});}
            var Q2;
            {var subQ5=sQuery(id+"F0.wireOp",EDGE,"E575");Q2=makeQuery(id+"F0.imprint","IMPRINT",FACE,{"disambiguationData":[TD([[makeQuery(id+"F0.imprint","IMPRINT",EDGE,{"derivedFrom":subQ5}),1.0]])]});}
            var Q3;
            {var subQ0=sQuery(id+"F0.wireOp",EDGE,"E574");var subQ1=sQuery(id+"F0.wireOp",EDGE,"E538.trimOffspring");var subQ2=makeQuery(id+"F0.imprint","INTERSECT",VERTEX,{"derivedFrom":[subQ1,subQ0]});Q3=makeQuery(id+"F0.imprint","IMPRINT",FACE,{"disambiguationData":[TD([[makeQuery(id+"F0.imprint","IMPRINT",EDGE,{"disambiguationData":[TD([[subQ2,-1.0]])],"derivedFrom":subQ1}),1.0]])]});}
            var Q4;
            {var subQ5=sQuery(id+"F0.wireOp",EDGE,"E573");Q4=makeQuery(id+"F0.imprint","IMPRINT",FACE,{"disambiguationData":[TD([[makeQuery(id+"F0.imprint","IMPRINT",EDGE,{"derivedFrom":subQ5}),-1.0]])]});}
            extrude(context, id + "F9", {"entities" : qUnion([Q0, Q1, Q2, Q3, Q4]), "operationType" : NewBodyOperationType.REMOVE, "depth" : 15.8 * mm});
        }
        {
            var Q0;
            {var subQ7=sQuery(id+"F0.wireOp",EDGE,"E559");var subQ8=sQuery(id+"F0.wireOp",EDGE,"E537");var subQ9=makeQuery(id+"F0.imprint","INTERSECT",VERTEX,{"derivedFrom":[subQ8,subQ7]});Q0=makeQuery(id+"F0.imprint","IMPRINT",FACE,{"disambiguationData":[TD([[makeQuery(id+"F0.imprint","IMPRINT",EDGE,{"disambiguationData":[TD([[subQ9,-1.0]])],"derivedFrom":subQ8}),1.0]])]});}
            var Q1;
            {var subQ0=sQuery(id+"F0.wireOp",EDGE,"E565");Q1=makeQuery(id+"F0.imprint","IMPRINT",FACE,{"disambiguationData":[TD([[makeQuery(id+"F0.imprint","IMPRINT",EDGE,{"derivedFrom":subQ0}),-1.0]])]});}
            var Q2;
            {var subQ0=sQuery(id+"F0.wireOp",EDGE,"E576");var subQ1=sQuery(id+"F0.wireOp",EDGE,"E537");var subQ2=makeQuery(id+"F0.imprint","INTERSECT",VERTEX,{"derivedFrom":[subQ1,subQ0]});Q2=makeQuery(id+"F0.imprint","IMPRINT",FACE,{"disambiguationData":[TD([[makeQuery(id+"F0.imprint","IMPRINT",EDGE,{"disambiguationData":[TD([[subQ2,1.0]])],"derivedFrom":subQ1}),1.0]])]});}
            var Q3;
            {var subQ0=sQuery(id+"F0.wireOp",EDGE,"E572");var subQ1=sQuery(id+"F0.wireOp",EDGE,"E543.MirrorCS");var subQ2=makeQuery(id+"F0.imprint","INTERSECT",VERTEX,{"derivedFrom":[subQ1,subQ0]});Q3=makeQuery(id+"F0.imprint","IMPRINT",FACE,{"disambiguationData":[TD([[makeQuery(id+"F0.imprint","IMPRINT",EDGE,{"disambiguationData":[TD([[subQ2,1.0]])],"derivedFrom":subQ1}),-1.0]])]});}
            extrude(context, id + "F10", {"entities" : qUnion([Q0, Q1, Q2, Q3]), "operationType" : NewBodyOperationType.ADD, "depth" : 1.5 * mm});
        }
    });
